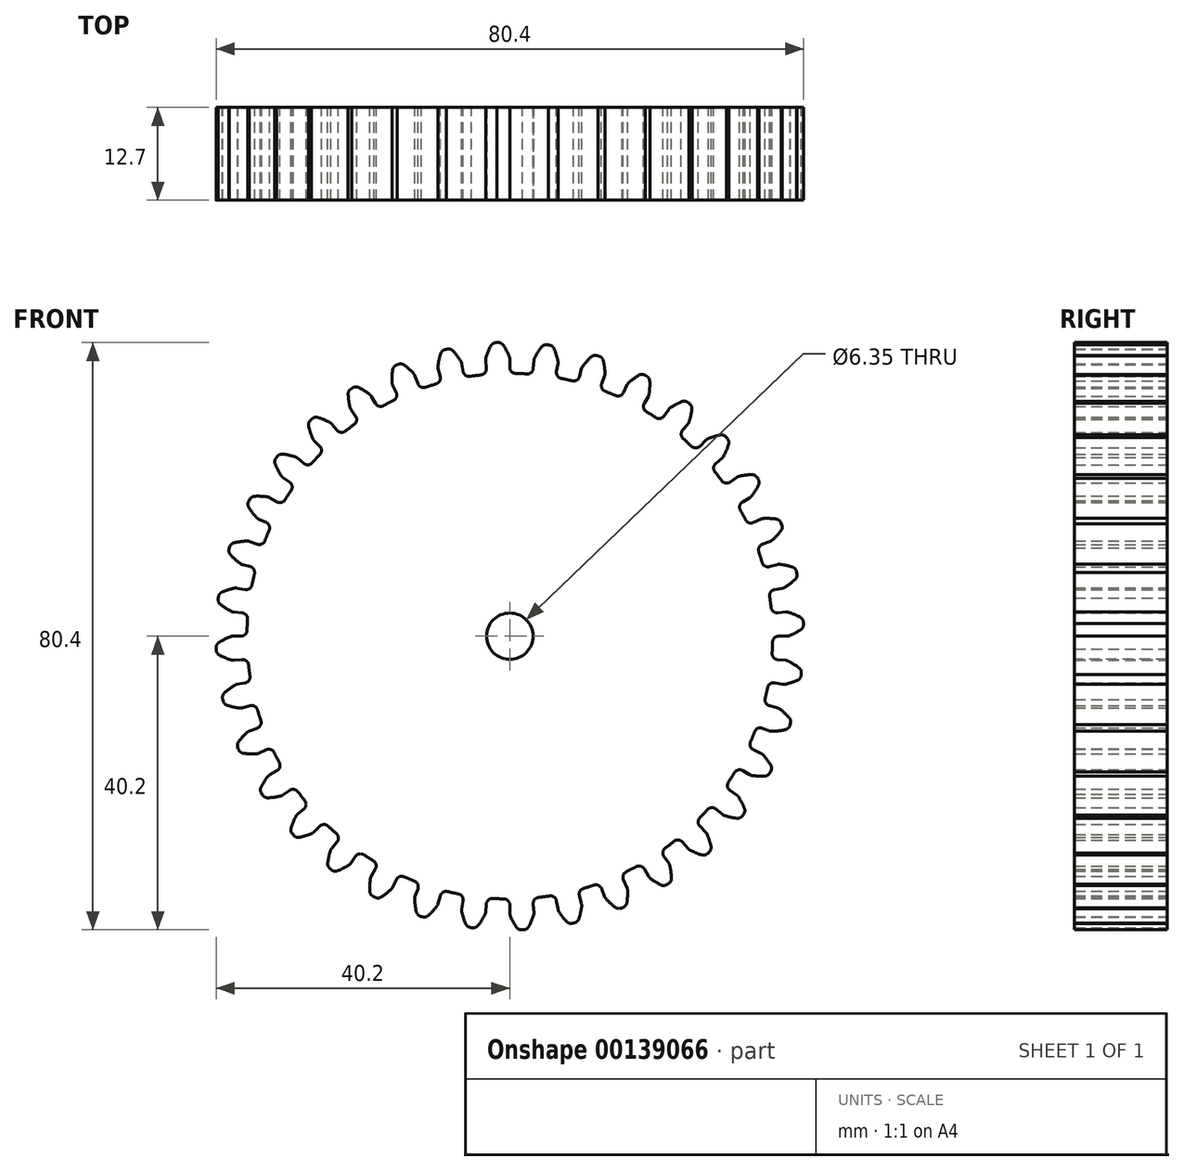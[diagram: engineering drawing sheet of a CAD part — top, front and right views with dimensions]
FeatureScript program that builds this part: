
annotation { "Feature Type Name" : "Feature", "Feature Type Description" : "" }
export const myFeature = defineFeature(function(context is Context, id is Id, definition is map)
    precondition{}
    {
        {
            var Q0;
            Q0=qCreatedBy(makeId("Front.planeOp"),FACE);
            var sketch = newSketch(context, id + "F0", { "sketchPlane" : qUnion([Q0])});
            skArc(sketch, "E0", {"start": v(-3.94, 35.77) * mm, "mid": v(-4.7, 35.68) * mm, "end": v(-5.45, 35.57) * mm});
            skLineSegment(sketch, "E1", {"start": v(-1.57, 40.2) * mm, "end": v(-1.76, 40.2) * mm});
            skLineSegment(sketch, "E2", {"start": v(0, 37.94) * mm, "end": v(0, 36.8) * mm});
            skArc(sketch, "E3.trimOffspring", {"start": v(-0.06, 38.25) * mm, "mid": v(-0.43, 39.06) * mm, "end": v(-0.87, 39.82) * mm});
            skLineSegment(sketch, "E4.MirrorCS", {"start": v(-1.94, 40.18) * mm, "end": v(-1.76, 40.2) * mm});
            skArc(sketch, "E5.MirrorCS", {"start": v(-3.27, 38.11) * mm, "mid": v(-2.98, 38.94) * mm, "end": v(-2.6, 39.75) * mm});
            skLineSegment(sketch, "E6.MirrorCS", {"start": v(-3.3, 37.8) * mm, "end": v(-3.2, 36.66) * mm});
            skPoint(sketch, "E7.visualSharp", {"position": v(0, 35.98) * mm});
            skArc(sketch, "E7.filletArc", {"start": v(0, 36.8) * mm, "mid": v(0.24, 36.22) * mm, "end": v(0.8, 35.97) * mm});
            skPoint(sketch, "E8.visualSharp", {"position": v(-3.14, 35.85) * mm});
            skArc(sketch, "E8.filletArc", {"start": v(-3.94, 35.77) * mm, "mid": v(-3.4, 36.06) * mm, "end": v(-3.2, 36.66) * mm});
            skPoint(sketch, "E9.visualSharp", {"position": v(-3.32, 37.96) * mm});
            skArc(sketch, "E9.filletArc", {"start": v(-3.27, 38.11) * mm, "mid": v(-3.3, 37.96) * mm, "end": v(-3.3, 37.8) * mm});
            skPoint(sketch, "E10.visualSharp", {"position": v(0, 38.1) * mm});
            skArc(sketch, "E10.filletArc", {"start": v(0, 37.94) * mm, "mid": v(-0.02, 38.1) * mm, "end": v(-0.06, 38.25) * mm});
            skPoint(sketch, "E11.visualSharp", {"position": v(-2.38, 40.15) * mm});
            skArc(sketch, "E11.filletArc", {"start": v(-1.94, 40.18) * mm, "mid": v(-2.33, 40.05) * mm, "end": v(-2.6, 39.75) * mm});
            skPoint(sketch, "E12.visualSharp", {"position": v(-1.13, 40.2) * mm});
            skArc(sketch, "E12.filletArc", {"start": v(-0.87, 39.82) * mm, "mid": v(-1.17, 40.1) * mm, "end": v(-1.57, 40.2) * mm});
            skArc(sketch, "E13.1.0", {"start": v(-10.1, 34.54) * mm, "mid": v(-9.6, 34.93) * mm, "end": v(-9.52, 35.55) * mm});
            skLineSegment(sketch, "E13.1.1", {"start": v(-9.82, 36.65) * mm, "end": v(-9.52, 35.55) * mm});
            skArc(sketch, "E13.1.2", {"start": v(-9.84, 36.96) * mm, "mid": v(-9.85, 36.8) * mm, "end": v(-9.82, 36.65) * mm});
            skArc(sketch, "E13.1.3", {"start": v(-9.84, 36.96) * mm, "mid": v(-9.7, 37.84) * mm, "end": v(-9.47, 38.69) * mm});
            skArc(sketch, "E13.1.4", {"start": v(-8.9, 39.24) * mm, "mid": v(-9.25, 39.04) * mm, "end": v(-9.47, 38.69) * mm});
            skLineSegment(sketch, "E13.1.5", {"start": v(-8.9, 39.24) * mm, "end": v(-8.7, 39.29) * mm});
            skLineSegment(sketch, "E13.1.6", {"start": v(-8.52, 39.32) * mm, "end": v(-8.7, 39.29) * mm});
            skArc(sketch, "E13.1.7", {"start": v(-7.77, 39.06) * mm, "mid": v(-8.12, 39.29) * mm, "end": v(-8.52, 39.32) * mm});
            skArc(sketch, "E13.1.8", {"start": v(-6.7, 37.66) * mm, "mid": v(-7.2, 38.39) * mm, "end": v(-7.77, 39.06) * mm});
            skArc(sketch, "E13.1.9", {"start": v(-6.59, 37.37) * mm, "mid": v(-6.63, 37.52) * mm, "end": v(-6.7, 37.66) * mm});
            skLineSegment(sketch, "E13.1.10", {"start": v(-6.59, 37.37) * mm, "end": v(-6.4, 36.24) * mm});
            skArc(sketch, "E13.1.11", {"start": v(-6.4, 36.24) * mm, "mid": v(-6.06, 35.71) * mm, "end": v(-5.45, 35.57) * mm});
            skArc(sketch, "E13.2.0", {"start": v(-15.93, 32.26) * mm, "mid": v(-15.52, 32.73) * mm, "end": v(-15.55, 33.35) * mm});
            skLineSegment(sketch, "E13.2.1", {"start": v(-16.04, 34.39) * mm, "end": v(-15.55, 33.35) * mm});
            skArc(sketch, "E13.2.2", {"start": v(-16.11, 34.7) * mm, "mid": v(-16.09, 34.54) * mm, "end": v(-16.04, 34.39) * mm});
            skArc(sketch, "E13.2.3", {"start": v(-16.11, 34.7) * mm, "mid": v(-16.12, 35.58) * mm, "end": v(-16.04, 36.46) * mm});
            skArc(sketch, "E13.2.4", {"start": v(-15.57, 37.1) * mm, "mid": v(-15.89, 36.84) * mm, "end": v(-16.04, 36.46) * mm});
            skLineSegment(sketch, "E13.2.5", {"start": v(-15.57, 37.1) * mm, "end": v(-15.4, 37.18) * mm});
            skLineSegment(sketch, "E13.2.6", {"start": v(-15.22, 37.24) * mm, "end": v(-15.4, 37.18) * mm});
            skArc(sketch, "E13.2.7", {"start": v(-14.44, 37.12) * mm, "mid": v(-14.81, 37.28) * mm, "end": v(-15.22, 37.24) * mm});
            skArc(sketch, "E13.2.8", {"start": v(-13.14, 35.93) * mm, "mid": v(-13.76, 36.55) * mm, "end": v(-14.44, 37.12) * mm});
            skArc(sketch, "E13.2.9", {"start": v(-12.98, 35.65) * mm, "mid": v(-13.05, 35.8) * mm, "end": v(-13.14, 35.93) * mm});
            skLineSegment(sketch, "E13.2.10", {"start": v(-12.98, 35.65) * mm, "end": v(-12.59, 34.58) * mm});
            skArc(sketch, "E13.2.11", {"start": v(-12.59, 34.58) * mm, "mid": v(-12.17, 34.12) * mm, "end": v(-11.55, 34.08) * mm});
            skArc(sketch, "E13.3.0", {"start": v(-21.3, 29) * mm, "mid": v(-20.97, 29.54) * mm, "end": v(-21.1, 30.14) * mm});
            skLineSegment(sketch, "E13.3.1", {"start": v(-21.76, 31.08) * mm, "end": v(-21.1, 30.14) * mm});
            skArc(sketch, "E13.3.2", {"start": v(-21.9, 31.37) * mm, "mid": v(-21.84, 31.22) * mm, "end": v(-21.76, 31.08) * mm});
            skArc(sketch, "E13.3.3", {"start": v(-21.9, 31.37) * mm, "mid": v(-22.05, 32.24) * mm, "end": v(-22.13, 33.12) * mm});
            skArc(sketch, "E13.3.4", {"start": v(-21.78, 33.83) * mm, "mid": v(-22.04, 33.52) * mm, "end": v(-22.13, 33.12) * mm});
            skLineSegment(sketch, "E13.3.5", {"start": v(-21.78, 33.83) * mm, "end": v(-21.62, 33.94) * mm});
            skLineSegment(sketch, "E13.3.6", {"start": v(-21.46, 34.03) * mm, "end": v(-21.62, 33.94) * mm});
            skArc(sketch, "E13.3.7", {"start": v(-20.66, 34.05) * mm, "mid": v(-21.06, 34.14) * mm, "end": v(-21.46, 34.03) * mm});
            skArc(sketch, "E13.3.8", {"start": v(-19.18, 33.1) * mm, "mid": v(-19.9, 33.6) * mm, "end": v(-20.66, 34.05) * mm});
            skArc(sketch, "E13.3.9", {"start": v(-18.97, 32.86) * mm, "mid": v(-19.06, 32.99) * mm, "end": v(-19.18, 33.1) * mm});
            skLineSegment(sketch, "E13.3.10", {"start": v(-18.97, 32.86) * mm, "end": v(-18.4, 31.87) * mm});
            skArc(sketch, "E13.3.11", {"start": v(-18.4, 31.87) * mm, "mid": v(-17.9, 31.49) * mm, "end": v(-17.29, 31.56) * mm});
            skArc(sketch, "E13.4.0", {"start": v(-26, 24.87) * mm, "mid": v(-25.78, 25.45) * mm, "end": v(-26.02, 26.02) * mm});
            skLineSegment(sketch, "E13.4.1", {"start": v(-26.83, 26.83) * mm, "end": v(-26.02, 26.02) * mm});
            skArc(sketch, "E13.4.2", {"start": v(-27, 27.1) * mm, "mid": v(-26.93, 26.95) * mm, "end": v(-26.83, 26.83) * mm});
            skArc(sketch, "E13.4.3", {"start": v(-27, 27.1) * mm, "mid": v(-27.31, 27.92) * mm, "end": v(-27.54, 28.77) * mm});
            skArc(sketch, "E13.4.4", {"start": v(-27.32, 29.53) * mm, "mid": v(-27.53, 29.18) * mm, "end": v(-27.54, 28.77) * mm});
            skLineSegment(sketch, "E13.4.5", {"start": v(-27.32, 29.53) * mm, "end": v(-27.19, 29.67) * mm});
            skLineSegment(sketch, "E13.4.6", {"start": v(-27.04, 29.79) * mm, "end": v(-27.19, 29.67) * mm});
            skArc(sketch, "E13.4.7", {"start": v(-26.26, 29.94) * mm, "mid": v(-26.67, 29.97) * mm, "end": v(-27.04, 29.79) * mm});
            skArc(sketch, "E13.4.8", {"start": v(-24.63, 29.26) * mm, "mid": v(-25.43, 29.64) * mm, "end": v(-26.26, 29.94) * mm});
            skArc(sketch, "E13.4.9", {"start": v(-24.39, 29.07) * mm, "mid": v(-24.5, 29.18) * mm, "end": v(-24.63, 29.26) * mm});
            skLineSegment(sketch, "E13.4.10", {"start": v(-24.39, 29.07) * mm, "end": v(-23.65, 28.2) * mm});
            skArc(sketch, "E13.4.11", {"start": v(-23.65, 28.2) * mm, "mid": v(-23.1, 27.9) * mm, "end": v(-22.5, 28.08) * mm});
            skArc(sketch, "E13.5.0", {"start": v(-29.93, 19.97) * mm, "mid": v(-29.8, 20.58) * mm, "end": v(-30.14, 21.1) * mm});
            skLineSegment(sketch, "E13.5.1", {"start": v(-31.08, 21.76) * mm, "end": v(-30.14, 21.1) * mm});
            skArc(sketch, "E13.5.2", {"start": v(-31.3, 22) * mm, "mid": v(-31.2, 21.87) * mm, "end": v(-31.08, 21.76) * mm});
            skArc(sketch, "E13.5.3", {"start": v(-31.3, 22) * mm, "mid": v(-31.75, 22.75) * mm, "end": v(-32.12, 23.55) * mm});
            skArc(sketch, "E13.5.4", {"start": v(-32.03, 24.34) * mm, "mid": v(-32.18, 23.96) * mm, "end": v(-32.12, 23.55) * mm});
            skLineSegment(sketch, "E13.5.5", {"start": v(-32.03, 24.34) * mm, "end": v(-31.92, 24.5) * mm});
            skLineSegment(sketch, "E13.5.6", {"start": v(-31.8, 24.64) * mm, "end": v(-31.92, 24.5) * mm});
            skArc(sketch, "E13.5.7", {"start": v(-31.06, 24.93) * mm, "mid": v(-31.47, 24.88) * mm, "end": v(-31.8, 24.64) * mm});
            skArc(sketch, "E13.5.8", {"start": v(-29.34, 24.54) * mm, "mid": v(-30.2, 24.78) * mm, "end": v(-31.06, 24.93) * mm});
            skArc(sketch, "E13.5.9", {"start": v(-29.07, 24.39) * mm, "mid": v(-29.2, 24.48) * mm, "end": v(-29.34, 24.54) * mm});
            skLineSegment(sketch, "E13.5.10", {"start": v(-29.07, 24.39) * mm, "end": v(-28.2, 23.65) * mm});
            skArc(sketch, "E13.5.11", {"start": v(-28.2, 23.65) * mm, "mid": v(-27.6, 23.46) * mm, "end": v(-27.04, 23.74) * mm});
            skArc(sketch, "E13.6.0", {"start": v(-32.94, 14.47) * mm, "mid": v(-32.93, 15.1) * mm, "end": v(-33.35, 15.55) * mm});
            skLineSegment(sketch, "E13.6.1", {"start": v(-34.39, 16.04) * mm, "end": v(-33.35, 15.55) * mm});
            skArc(sketch, "E13.6.2", {"start": v(-34.64, 16.22) * mm, "mid": v(-34.52, 16.12) * mm, "end": v(-34.39, 16.04) * mm});
            skArc(sketch, "E13.6.3", {"start": v(-34.64, 16.22) * mm, "mid": v(-35.21, 16.9) * mm, "end": v(-35.72, 17.62) * mm});
            skArc(sketch, "E13.6.4", {"start": v(-35.77, 18.4) * mm, "mid": v(-35.85, 18) * mm, "end": v(-35.72, 17.62) * mm});
            skLineSegment(sketch, "E13.6.5", {"start": v(-35.77, 18.4) * mm, "end": v(-35.7, 18.58) * mm});
            skLineSegment(sketch, "E13.6.6", {"start": v(-35.6, 18.74) * mm, "end": v(-35.7, 18.58) * mm});
            skArc(sketch, "E13.6.7", {"start": v(-34.92, 19.16) * mm, "mid": v(-35.31, 19.04) * mm, "end": v(-35.6, 18.74) * mm});
            skArc(sketch, "E13.6.8", {"start": v(-33.16, 19.07) * mm, "mid": v(-34.04, 19.16) * mm, "end": v(-34.92, 19.16) * mm});
            skArc(sketch, "E13.6.9", {"start": v(-32.86, 18.97) * mm, "mid": v(-33, 19.04) * mm, "end": v(-33.16, 19.07) * mm});
            skLineSegment(sketch, "E13.6.10", {"start": v(-32.86, 18.97) * mm, "end": v(-31.87, 18.4) * mm});
            skArc(sketch, "E13.6.11", {"start": v(-31.87, 18.4) * mm, "mid": v(-31.25, 18.31) * mm, "end": v(-30.75, 18.69) * mm});
            skArc(sketch, "E13.7.0", {"start": v(-34.96, 8.53) * mm, "mid": v(-35.05, 9.15) * mm, "end": v(-35.55, 9.52) * mm});
            skLineSegment(sketch, "E13.7.1", {"start": v(-36.65, 9.82) * mm, "end": v(-35.55, 9.52) * mm});
            skArc(sketch, "E13.7.2", {"start": v(-36.93, 9.96) * mm, "mid": v(-36.8, 9.88) * mm, "end": v(-36.65, 9.82) * mm});
            skArc(sketch, "E13.7.3", {"start": v(-36.93, 9.96) * mm, "mid": v(-37.61, 10.52) * mm, "end": v(-38.24, 11.15) * mm});
            skArc(sketch, "E13.7.4", {"start": v(-38.43, 11.92) * mm, "mid": v(-38.43, 11.5) * mm, "end": v(-38.24, 11.15) * mm});
            skLineSegment(sketch, "E13.7.5", {"start": v(-38.43, 11.92) * mm, "end": v(-38.38, 12.1) * mm});
            skLineSegment(sketch, "E13.7.6", {"start": v(-38.31, 12.28) * mm, "end": v(-38.38, 12.1) * mm});
            skArc(sketch, "E13.7.7", {"start": v(-37.72, 12.8) * mm, "mid": v(-38.08, 12.62) * mm, "end": v(-38.31, 12.28) * mm});
            skArc(sketch, "E13.7.8", {"start": v(-35.97, 13.03) * mm, "mid": v(-36.85, 12.95) * mm, "end": v(-37.72, 12.8) * mm});
            skArc(sketch, "E13.7.9", {"start": v(-35.65, 12.98) * mm, "mid": v(-35.8, 13.02) * mm, "end": v(-35.97, 13.03) * mm});
            skLineSegment(sketch, "E13.7.10", {"start": v(-35.65, 12.98) * mm, "end": v(-34.58, 12.59) * mm});
            skArc(sketch, "E13.7.11", {"start": v(-34.58, 12.59) * mm, "mid": v(-33.96, 12.6) * mm, "end": v(-33.53, 13.06) * mm});
            skArc(sketch, "E13.8.0", {"start": v(-35.9, 2.33) * mm, "mid": v(-36.1, 2.92) * mm, "end": v(-36.66, 3.2) * mm});
            skLineSegment(sketch, "E13.8.1", {"start": v(-37.8, 3.3) * mm, "end": v(-36.66, 3.2) * mm});
            skArc(sketch, "E13.8.2", {"start": v(-38.1, 3.4) * mm, "mid": v(-37.95, 3.34) * mm, "end": v(-37.8, 3.3) * mm});
            skArc(sketch, "E13.8.3", {"start": v(-38.1, 3.4) * mm, "mid": v(-38.87, 3.83) * mm, "end": v(-39.6, 4.34) * mm});
            skArc(sketch, "E13.8.4", {"start": v(-39.91, 5.06) * mm, "mid": v(-39.85, 4.66) * mm, "end": v(-39.6, 4.34) * mm});
            skLineSegment(sketch, "E13.8.5", {"start": v(-39.91, 5.06) * mm, "end": v(-39.9, 5.25) * mm});
            skLineSegment(sketch, "E13.8.6", {"start": v(-39.86, 5.44) * mm, "end": v(-39.9, 5.25) * mm});
            skArc(sketch, "E13.8.7", {"start": v(-39.37, 6.06) * mm, "mid": v(-39.7, 5.81) * mm, "end": v(-39.86, 5.44) * mm});
            skArc(sketch, "E13.8.8", {"start": v(-37.68, 6.58) * mm, "mid": v(-38.54, 6.36) * mm, "end": v(-39.37, 6.06) * mm});
            skArc(sketch, "E13.8.9", {"start": v(-37.37, 6.59) * mm, "mid": v(-37.52, 6.6) * mm, "end": v(-37.68, 6.58) * mm});
            skLineSegment(sketch, "E13.8.10", {"start": v(-37.37, 6.59) * mm, "end": v(-36.24, 6.4) * mm});
            skArc(sketch, "E13.8.11", {"start": v(-36.24, 6.4) * mm, "mid": v(-35.63, 6.52) * mm, "end": v(-35.29, 7.04) * mm});
            skArc(sketch, "E13.9.0", {"start": v(-35.77, -3.94) * mm, "mid": v(-36.06, -3.4) * mm, "end": v(-36.66, -3.2) * mm});
            skLineSegment(sketch, "E13.9.1", {"start": v(-37.8, -3.3) * mm, "end": v(-36.66, -3.2) * mm});
            skArc(sketch, "E13.9.2", {"start": v(-38.11, -3.27) * mm, "mid": v(-37.96, -3.3) * mm, "end": v(-37.8, -3.3) * mm});
            skArc(sketch, "E13.9.3", {"start": v(-38.11, -3.27) * mm, "mid": v(-38.94, -2.98) * mm, "end": v(-39.75, -2.6) * mm});
            skArc(sketch, "E13.9.4", {"start": v(-40.18, -1.94) * mm, "mid": v(-40.05, -2.33) * mm, "end": v(-39.75, -2.6) * mm});
            skLineSegment(sketch, "E13.9.5", {"start": v(-40.18, -1.94) * mm, "end": v(-40.2, -1.76) * mm});
            skLineSegment(sketch, "E13.9.6", {"start": v(-40.2, -1.57) * mm, "end": v(-40.2, -1.76) * mm});
            skArc(sketch, "E13.9.7", {"start": v(-39.82, -0.87) * mm, "mid": v(-40.1, -1.17) * mm, "end": v(-40.2, -1.57) * mm});
            skArc(sketch, "E13.9.8", {"start": v(-38.25, -0.06) * mm, "mid": v(-39.06, -0.43) * mm, "end": v(-39.82, -0.87) * mm});
            skArc(sketch, "E13.9.9", {"start": v(-37.94, 0) * mm, "mid": v(-38.1, -0.02) * mm, "end": v(-38.25, -0.06) * mm});
            skLineSegment(sketch, "E13.9.10", {"start": v(-37.94, 0) * mm, "end": v(-36.8, 0) * mm});
            skArc(sketch, "E13.9.11", {"start": v(-36.8, 0) * mm, "mid": v(-36.22, 0.24) * mm, "end": v(-35.97, 0.8) * mm});
            skArc(sketch, "E13.10.0", {"start": v(-34.54, -10.1) * mm, "mid": v(-34.93, -9.6) * mm, "end": v(-35.55, -9.52) * mm});
            skLineSegment(sketch, "E13.10.1", {"start": v(-36.65, -9.82) * mm, "end": v(-35.55, -9.52) * mm});
            skArc(sketch, "E13.10.2", {"start": v(-36.96, -9.84) * mm, "mid": v(-36.8, -9.85) * mm, "end": v(-36.65, -9.82) * mm});
            skArc(sketch, "E13.10.3", {"start": v(-36.96, -9.84) * mm, "mid": v(-37.84, -9.7) * mm, "end": v(-38.69, -9.47) * mm});
            skArc(sketch, "E13.10.4", {"start": v(-39.24, -8.9) * mm, "mid": v(-39.04, -9.25) * mm, "end": v(-38.69, -9.47) * mm});
            skLineSegment(sketch, "E13.10.5", {"start": v(-39.24, -8.9) * mm, "end": v(-39.29, -8.7) * mm});
            skLineSegment(sketch, "E13.10.6", {"start": v(-39.32, -8.52) * mm, "end": v(-39.29, -8.7) * mm});
            skArc(sketch, "E13.10.7", {"start": v(-39.06, -7.77) * mm, "mid": v(-39.29, -8.12) * mm, "end": v(-39.32, -8.52) * mm});
            skArc(sketch, "E13.10.8", {"start": v(-37.66, -6.7) * mm, "mid": v(-38.39, -7.2) * mm, "end": v(-39.06, -7.77) * mm});
            skArc(sketch, "E13.10.9", {"start": v(-37.37, -6.59) * mm, "mid": v(-37.52, -6.63) * mm, "end": v(-37.66, -6.7) * mm});
            skLineSegment(sketch, "E13.10.10", {"start": v(-37.37, -6.59) * mm, "end": v(-36.24, -6.4) * mm});
            skArc(sketch, "E13.10.11", {"start": v(-36.24, -6.4) * mm, "mid": v(-35.71, -6.06) * mm, "end": v(-35.57, -5.45) * mm});
            skArc(sketch, "E13.11.0", {"start": v(-32.26, -15.93) * mm, "mid": v(-32.73, -15.52) * mm, "end": v(-33.35, -15.55) * mm});
            skLineSegment(sketch, "E13.11.1", {"start": v(-34.39, -16.04) * mm, "end": v(-33.35, -15.55) * mm});
            skArc(sketch, "E13.11.2", {"start": v(-34.7, -16.11) * mm, "mid": v(-34.54, -16.09) * mm, "end": v(-34.39, -16.04) * mm});
            skArc(sketch, "E13.11.3", {"start": v(-34.7, -16.11) * mm, "mid": v(-35.58, -16.12) * mm, "end": v(-36.46, -16.04) * mm});
            skArc(sketch, "E13.11.4", {"start": v(-37.1, -15.57) * mm, "mid": v(-36.84, -15.89) * mm, "end": v(-36.46, -16.04) * mm});
            skLineSegment(sketch, "E13.11.5", {"start": v(-37.1, -15.57) * mm, "end": v(-37.18, -15.4) * mm});
            skLineSegment(sketch, "E13.11.6", {"start": v(-37.24, -15.22) * mm, "end": v(-37.18, -15.4) * mm});
            skArc(sketch, "E13.11.7", {"start": v(-37.12, -14.44) * mm, "mid": v(-37.28, -14.81) * mm, "end": v(-37.24, -15.22) * mm});
            skArc(sketch, "E13.11.8", {"start": v(-35.93, -13.14) * mm, "mid": v(-36.55, -13.76) * mm, "end": v(-37.12, -14.44) * mm});
            skArc(sketch, "E13.11.9", {"start": v(-35.65, -12.98) * mm, "mid": v(-35.8, -13.05) * mm, "end": v(-35.93, -13.14) * mm});
            skLineSegment(sketch, "E13.11.10", {"start": v(-35.65, -12.98) * mm, "end": v(-34.58, -12.59) * mm});
            skArc(sketch, "E13.11.11", {"start": v(-34.58, -12.59) * mm, "mid": v(-34.12, -12.17) * mm, "end": v(-34.08, -11.55) * mm});
            skArc(sketch, "E13.12.0", {"start": v(-29, -21.3) * mm, "mid": v(-29.54, -20.97) * mm, "end": v(-30.14, -21.1) * mm});
            skLineSegment(sketch, "E13.12.1", {"start": v(-31.08, -21.76) * mm, "end": v(-30.14, -21.1) * mm});
            skArc(sketch, "E13.12.2", {"start": v(-31.37, -21.9) * mm, "mid": v(-31.22, -21.84) * mm, "end": v(-31.08, -21.76) * mm});
            skArc(sketch, "E13.12.3", {"start": v(-31.37, -21.9) * mm, "mid": v(-32.24, -22.05) * mm, "end": v(-33.12, -22.13) * mm});
            skArc(sketch, "E13.12.4", {"start": v(-33.83, -21.78) * mm, "mid": v(-33.52, -22.04) * mm, "end": v(-33.12, -22.13) * mm});
            skLineSegment(sketch, "E13.12.5", {"start": v(-33.83, -21.78) * mm, "end": v(-33.94, -21.62) * mm});
            skLineSegment(sketch, "E13.12.6", {"start": v(-34.03, -21.46) * mm, "end": v(-33.94, -21.62) * mm});
            skArc(sketch, "E13.12.7", {"start": v(-34.05, -20.66) * mm, "mid": v(-34.14, -21.06) * mm, "end": v(-34.03, -21.46) * mm});
            skArc(sketch, "E13.12.8", {"start": v(-33.1, -19.18) * mm, "mid": v(-33.6, -19.9) * mm, "end": v(-34.05, -20.66) * mm});
            skArc(sketch, "E13.12.9", {"start": v(-32.86, -18.97) * mm, "mid": v(-32.99, -19.06) * mm, "end": v(-33.1, -19.18) * mm});
            skLineSegment(sketch, "E13.12.10", {"start": v(-32.86, -18.97) * mm, "end": v(-31.87, -18.4) * mm});
            skArc(sketch, "E13.12.11", {"start": v(-31.87, -18.4) * mm, "mid": v(-31.49, -17.9) * mm, "end": v(-31.56, -17.29) * mm});
            skArc(sketch, "E13.13.0", {"start": v(-24.87, -26) * mm, "mid": v(-25.45, -25.78) * mm, "end": v(-26.02, -26.02) * mm});
            skLineSegment(sketch, "E13.13.1", {"start": v(-26.83, -26.83) * mm, "end": v(-26.02, -26.02) * mm});
            skArc(sketch, "E13.13.2", {"start": v(-27.1, -27) * mm, "mid": v(-26.95, -26.93) * mm, "end": v(-26.83, -26.83) * mm});
            skArc(sketch, "E13.13.3", {"start": v(-27.1, -27) * mm, "mid": v(-27.92, -27.31) * mm, "end": v(-28.77, -27.54) * mm});
            skArc(sketch, "E13.13.4", {"start": v(-29.53, -27.32) * mm, "mid": v(-29.18, -27.53) * mm, "end": v(-28.77, -27.54) * mm});
            skLineSegment(sketch, "E13.13.5", {"start": v(-29.53, -27.32) * mm, "end": v(-29.67, -27.19) * mm});
            skLineSegment(sketch, "E13.13.6", {"start": v(-29.79, -27.04) * mm, "end": v(-29.67, -27.19) * mm});
            skArc(sketch, "E13.13.7", {"start": v(-29.94, -26.26) * mm, "mid": v(-29.97, -26.67) * mm, "end": v(-29.79, -27.04) * mm});
            skArc(sketch, "E13.13.8", {"start": v(-29.26, -24.63) * mm, "mid": v(-29.64, -25.43) * mm, "end": v(-29.94, -26.26) * mm});
            skArc(sketch, "E13.13.9", {"start": v(-29.07, -24.39) * mm, "mid": v(-29.18, -24.5) * mm, "end": v(-29.26, -24.63) * mm});
            skLineSegment(sketch, "E13.13.10", {"start": v(-29.07, -24.39) * mm, "end": v(-28.2, -23.65) * mm});
            skArc(sketch, "E13.13.11", {"start": v(-28.2, -23.65) * mm, "mid": v(-27.9, -23.1) * mm, "end": v(-28.08, -22.5) * mm});
            skArc(sketch, "E13.14.0", {"start": v(-19.97, -29.93) * mm, "mid": v(-20.58, -29.8) * mm, "end": v(-21.1, -30.14) * mm});
            skLineSegment(sketch, "E13.14.1", {"start": v(-21.76, -31.08) * mm, "end": v(-21.1, -30.14) * mm});
            skArc(sketch, "E13.14.2", {"start": v(-22, -31.3) * mm, "mid": v(-21.87, -31.2) * mm, "end": v(-21.76, -31.08) * mm});
            skArc(sketch, "E13.14.3", {"start": v(-22, -31.3) * mm, "mid": v(-22.75, -31.75) * mm, "end": v(-23.55, -32.12) * mm});
            skArc(sketch, "E13.14.4", {"start": v(-24.34, -32.03) * mm, "mid": v(-23.96, -32.18) * mm, "end": v(-23.55, -32.12) * mm});
            skLineSegment(sketch, "E13.14.5", {"start": v(-24.34, -32.03) * mm, "end": v(-24.5, -31.92) * mm});
            skLineSegment(sketch, "E13.14.6", {"start": v(-24.64, -31.8) * mm, "end": v(-24.5, -31.92) * mm});
            skArc(sketch, "E13.14.7", {"start": v(-24.93, -31.06) * mm, "mid": v(-24.88, -31.47) * mm, "end": v(-24.64, -31.8) * mm});
            skArc(sketch, "E13.14.8", {"start": v(-24.54, -29.34) * mm, "mid": v(-24.78, -30.2) * mm, "end": v(-24.93, -31.06) * mm});
            skArc(sketch, "E13.14.9", {"start": v(-24.39, -29.07) * mm, "mid": v(-24.48, -29.2) * mm, "end": v(-24.54, -29.34) * mm});
            skLineSegment(sketch, "E13.14.10", {"start": v(-24.39, -29.07) * mm, "end": v(-23.65, -28.2) * mm});
            skArc(sketch, "E13.14.11", {"start": v(-23.65, -28.2) * mm, "mid": v(-23.46, -27.6) * mm, "end": v(-23.74, -27.04) * mm});
            skArc(sketch, "E13.15.0", {"start": v(-14.47, -32.94) * mm, "mid": v(-15.1, -32.93) * mm, "end": v(-15.55, -33.35) * mm});
            skLineSegment(sketch, "E13.15.1", {"start": v(-16.04, -34.39) * mm, "end": v(-15.55, -33.35) * mm});
            skArc(sketch, "E13.15.2", {"start": v(-16.22, -34.64) * mm, "mid": v(-16.12, -34.52) * mm, "end": v(-16.04, -34.39) * mm});
            skArc(sketch, "E13.15.3", {"start": v(-16.22, -34.64) * mm, "mid": v(-16.9, -35.21) * mm, "end": v(-17.62, -35.72) * mm});
            skArc(sketch, "E13.15.4", {"start": v(-18.4, -35.77) * mm, "mid": v(-18, -35.85) * mm, "end": v(-17.62, -35.72) * mm});
            skLineSegment(sketch, "E13.15.5", {"start": v(-18.4, -35.77) * mm, "end": v(-18.58, -35.7) * mm});
            skLineSegment(sketch, "E13.15.6", {"start": v(-18.74, -35.6) * mm, "end": v(-18.58, -35.7) * mm});
            skArc(sketch, "E13.15.7", {"start": v(-19.16, -34.92) * mm, "mid": v(-19.04, -35.31) * mm, "end": v(-18.74, -35.6) * mm});
            skArc(sketch, "E13.15.8", {"start": v(-19.07, -33.16) * mm, "mid": v(-19.16, -34.04) * mm, "end": v(-19.16, -34.92) * mm});
            skArc(sketch, "E13.15.9", {"start": v(-18.97, -32.86) * mm, "mid": v(-19.04, -33) * mm, "end": v(-19.07, -33.16) * mm});
            skLineSegment(sketch, "E13.15.10", {"start": v(-18.97, -32.86) * mm, "end": v(-18.4, -31.87) * mm});
            skArc(sketch, "E13.15.11", {"start": v(-18.4, -31.87) * mm, "mid": v(-18.31, -31.25) * mm, "end": v(-18.69, -30.75) * mm});
            skArc(sketch, "E13.16.0", {"start": v(-8.53, -34.96) * mm, "mid": v(-9.15, -35.05) * mm, "end": v(-9.52, -35.55) * mm});
            skLineSegment(sketch, "E13.16.1", {"start": v(-9.82, -36.65) * mm, "end": v(-9.52, -35.55) * mm});
            skArc(sketch, "E13.16.2", {"start": v(-9.96, -36.93) * mm, "mid": v(-9.88, -36.8) * mm, "end": v(-9.82, -36.65) * mm});
            skArc(sketch, "E13.16.3", {"start": v(-9.96, -36.93) * mm, "mid": v(-10.52, -37.61) * mm, "end": v(-11.15, -38.24) * mm});
            skArc(sketch, "E13.16.4", {"start": v(-11.92, -38.43) * mm, "mid": v(-11.5, -38.43) * mm, "end": v(-11.15, -38.24) * mm});
            skLineSegment(sketch, "E13.16.5", {"start": v(-11.92, -38.43) * mm, "end": v(-12.1, -38.38) * mm});
            skLineSegment(sketch, "E13.16.6", {"start": v(-12.28, -38.31) * mm, "end": v(-12.1, -38.38) * mm});
            skArc(sketch, "E13.16.7", {"start": v(-12.8, -37.72) * mm, "mid": v(-12.62, -38.08) * mm, "end": v(-12.28, -38.31) * mm});
            skArc(sketch, "E13.16.8", {"start": v(-13.03, -35.97) * mm, "mid": v(-12.95, -36.85) * mm, "end": v(-12.8, -37.72) * mm});
            skArc(sketch, "E13.16.9", {"start": v(-12.98, -35.65) * mm, "mid": v(-13.02, -35.8) * mm, "end": v(-13.03, -35.97) * mm});
            skLineSegment(sketch, "E13.16.10", {"start": v(-12.98, -35.65) * mm, "end": v(-12.59, -34.58) * mm});
            skArc(sketch, "E13.16.11", {"start": v(-12.59, -34.58) * mm, "mid": v(-12.6, -33.96) * mm, "end": v(-13.06, -33.53) * mm});
            skArc(sketch, "E13.17.0", {"start": v(-2.33, -35.9) * mm, "mid": v(-2.92, -36.1) * mm, "end": v(-3.2, -36.66) * mm});
            skLineSegment(sketch, "E13.17.1", {"start": v(-3.3, -37.8) * mm, "end": v(-3.2, -36.66) * mm});
            skArc(sketch, "E13.17.2", {"start": v(-3.4, -38.1) * mm, "mid": v(-3.34, -37.95) * mm, "end": v(-3.3, -37.8) * mm});
            skArc(sketch, "E13.17.3", {"start": v(-3.4, -38.1) * mm, "mid": v(-3.83, -38.87) * mm, "end": v(-4.34, -39.6) * mm});
            skArc(sketch, "E13.17.4", {"start": v(-5.06, -39.91) * mm, "mid": v(-4.66, -39.85) * mm, "end": v(-4.34, -39.6) * mm});
            skLineSegment(sketch, "E13.17.5", {"start": v(-5.06, -39.91) * mm, "end": v(-5.25, -39.9) * mm});
            skLineSegment(sketch, "E13.17.6", {"start": v(-5.44, -39.86) * mm, "end": v(-5.25, -39.9) * mm});
            skArc(sketch, "E13.17.7", {"start": v(-6.06, -39.37) * mm, "mid": v(-5.81, -39.7) * mm, "end": v(-5.44, -39.86) * mm});
            skArc(sketch, "E13.17.8", {"start": v(-6.58, -37.68) * mm, "mid": v(-6.36, -38.54) * mm, "end": v(-6.06, -39.37) * mm});
            skArc(sketch, "E13.17.9", {"start": v(-6.59, -37.37) * mm, "mid": v(-6.6, -37.52) * mm, "end": v(-6.58, -37.68) * mm});
            skLineSegment(sketch, "E13.17.10", {"start": v(-6.59, -37.37) * mm, "end": v(-6.4, -36.24) * mm});
            skArc(sketch, "E13.17.11", {"start": v(-6.4, -36.24) * mm, "mid": v(-6.52, -35.63) * mm, "end": v(-7.04, -35.29) * mm});
            skArc(sketch, "E13.18.0", {"start": v(3.94, -35.77) * mm, "mid": v(3.4, -36.06) * mm, "end": v(3.2, -36.66) * mm});
            skLineSegment(sketch, "E13.18.1", {"start": v(3.3, -37.8) * mm, "end": v(3.2, -36.66) * mm});
            skArc(sketch, "E13.18.2", {"start": v(3.27, -38.11) * mm, "mid": v(3.3, -37.96) * mm, "end": v(3.3, -37.8) * mm});
            skArc(sketch, "E13.18.3", {"start": v(3.27, -38.11) * mm, "mid": v(2.98, -38.94) * mm, "end": v(2.6, -39.75) * mm});
            skArc(sketch, "E13.18.4", {"start": v(1.94, -40.18) * mm, "mid": v(2.33, -40.05) * mm, "end": v(2.6, -39.75) * mm});
            skLineSegment(sketch, "E13.18.5", {"start": v(1.94, -40.18) * mm, "end": v(1.76, -40.2) * mm});
            skLineSegment(sketch, "E13.18.6", {"start": v(1.57, -40.2) * mm, "end": v(1.76, -40.2) * mm});
            skArc(sketch, "E13.18.7", {"start": v(0.87, -39.82) * mm, "mid": v(1.17, -40.1) * mm, "end": v(1.57, -40.2) * mm});
            skArc(sketch, "E13.18.8", {"start": v(0.06, -38.25) * mm, "mid": v(0.43, -39.06) * mm, "end": v(0.87, -39.82) * mm});
            skArc(sketch, "E13.18.9", {"start": v(0, -37.94) * mm, "mid": v(0.02, -38.1) * mm, "end": v(0.06, -38.25) * mm});
            skLineSegment(sketch, "E13.18.10", {"start": v(0, -37.94) * mm, "end": v(0, -36.8) * mm});
            skArc(sketch, "E13.18.11", {"start": v(0, -36.8) * mm, "mid": v(-0.24, -36.22) * mm, "end": v(-0.8, -35.97) * mm});
            skArc(sketch, "E13.19.0", {"start": v(10.1, -34.54) * mm, "mid": v(9.6, -34.93) * mm, "end": v(9.52, -35.55) * mm});
            skLineSegment(sketch, "E13.19.1", {"start": v(9.82, -36.65) * mm, "end": v(9.52, -35.55) * mm});
            skArc(sketch, "E13.19.2", {"start": v(9.84, -36.96) * mm, "mid": v(9.85, -36.8) * mm, "end": v(9.82, -36.65) * mm});
            skArc(sketch, "E13.19.3", {"start": v(9.84, -36.96) * mm, "mid": v(9.7, -37.84) * mm, "end": v(9.47, -38.69) * mm});
            skArc(sketch, "E13.19.4", {"start": v(8.9, -39.24) * mm, "mid": v(9.25, -39.04) * mm, "end": v(9.47, -38.69) * mm});
            skLineSegment(sketch, "E13.19.5", {"start": v(8.9, -39.24) * mm, "end": v(8.7, -39.29) * mm});
            skLineSegment(sketch, "E13.19.6", {"start": v(8.52, -39.32) * mm, "end": v(8.7, -39.29) * mm});
            skArc(sketch, "E13.19.7", {"start": v(7.77, -39.06) * mm, "mid": v(8.12, -39.29) * mm, "end": v(8.52, -39.32) * mm});
            skArc(sketch, "E13.19.8", {"start": v(6.7, -37.66) * mm, "mid": v(7.2, -38.39) * mm, "end": v(7.77, -39.06) * mm});
            skArc(sketch, "E13.19.9", {"start": v(6.59, -37.37) * mm, "mid": v(6.63, -37.52) * mm, "end": v(6.7, -37.66) * mm});
            skLineSegment(sketch, "E13.19.10", {"start": v(6.59, -37.37) * mm, "end": v(6.4, -36.24) * mm});
            skArc(sketch, "E13.19.11", {"start": v(6.4, -36.24) * mm, "mid": v(6.06, -35.71) * mm, "end": v(5.45, -35.57) * mm});
            skArc(sketch, "E13.20.0", {"start": v(15.93, -32.26) * mm, "mid": v(15.52, -32.73) * mm, "end": v(15.55, -33.35) * mm});
            skLineSegment(sketch, "E13.20.1", {"start": v(16.04, -34.39) * mm, "end": v(15.55, -33.35) * mm});
            skArc(sketch, "E13.20.2", {"start": v(16.11, -34.7) * mm, "mid": v(16.09, -34.54) * mm, "end": v(16.04, -34.39) * mm});
            skArc(sketch, "E13.20.3", {"start": v(16.11, -34.7) * mm, "mid": v(16.12, -35.58) * mm, "end": v(16.04, -36.46) * mm});
            skArc(sketch, "E13.20.4", {"start": v(15.57, -37.1) * mm, "mid": v(15.89, -36.84) * mm, "end": v(16.04, -36.46) * mm});
            skLineSegment(sketch, "E13.20.5", {"start": v(15.57, -37.1) * mm, "end": v(15.4, -37.18) * mm});
            skLineSegment(sketch, "E13.20.6", {"start": v(15.22, -37.24) * mm, "end": v(15.4, -37.18) * mm});
            skArc(sketch, "E13.20.7", {"start": v(14.44, -37.12) * mm, "mid": v(14.81, -37.28) * mm, "end": v(15.22, -37.24) * mm});
            skArc(sketch, "E13.20.8", {"start": v(13.14, -35.93) * mm, "mid": v(13.76, -36.55) * mm, "end": v(14.44, -37.12) * mm});
            skArc(sketch, "E13.20.9", {"start": v(12.98, -35.65) * mm, "mid": v(13.05, -35.8) * mm, "end": v(13.14, -35.93) * mm});
            skLineSegment(sketch, "E13.20.10", {"start": v(12.98, -35.65) * mm, "end": v(12.59, -34.58) * mm});
            skArc(sketch, "E13.20.11", {"start": v(12.59, -34.58) * mm, "mid": v(12.17, -34.12) * mm, "end": v(11.55, -34.08) * mm});
            skArc(sketch, "E13.21.0", {"start": v(21.3, -29) * mm, "mid": v(20.97, -29.54) * mm, "end": v(21.1, -30.14) * mm});
            skLineSegment(sketch, "E13.21.1", {"start": v(21.76, -31.08) * mm, "end": v(21.1, -30.14) * mm});
            skArc(sketch, "E13.21.2", {"start": v(21.9, -31.37) * mm, "mid": v(21.84, -31.22) * mm, "end": v(21.76, -31.08) * mm});
            skArc(sketch, "E13.21.3", {"start": v(21.9, -31.37) * mm, "mid": v(22.05, -32.24) * mm, "end": v(22.13, -33.12) * mm});
            skArc(sketch, "E13.21.4", {"start": v(21.78, -33.83) * mm, "mid": v(22.04, -33.52) * mm, "end": v(22.13, -33.12) * mm});
            skLineSegment(sketch, "E13.21.5", {"start": v(21.78, -33.83) * mm, "end": v(21.62, -33.94) * mm});
            skLineSegment(sketch, "E13.21.6", {"start": v(21.46, -34.03) * mm, "end": v(21.62, -33.94) * mm});
            skArc(sketch, "E13.21.7", {"start": v(20.66, -34.05) * mm, "mid": v(21.06, -34.14) * mm, "end": v(21.46, -34.03) * mm});
            skArc(sketch, "E13.21.8", {"start": v(19.18, -33.1) * mm, "mid": v(19.9, -33.6) * mm, "end": v(20.66, -34.05) * mm});
            skArc(sketch, "E13.21.9", {"start": v(18.97, -32.86) * mm, "mid": v(19.06, -32.99) * mm, "end": v(19.18, -33.1) * mm});
            skLineSegment(sketch, "E13.21.10", {"start": v(18.97, -32.86) * mm, "end": v(18.4, -31.87) * mm});
            skArc(sketch, "E13.21.11", {"start": v(18.4, -31.87) * mm, "mid": v(17.9, -31.49) * mm, "end": v(17.29, -31.56) * mm});
            skArc(sketch, "E13.22.0", {"start": v(26, -24.87) * mm, "mid": v(25.78, -25.45) * mm, "end": v(26.02, -26.02) * mm});
            skLineSegment(sketch, "E13.22.1", {"start": v(26.83, -26.83) * mm, "end": v(26.02, -26.02) * mm});
            skArc(sketch, "E13.22.2", {"start": v(27, -27.1) * mm, "mid": v(26.93, -26.95) * mm, "end": v(26.83, -26.83) * mm});
            skArc(sketch, "E13.22.3", {"start": v(27, -27.1) * mm, "mid": v(27.31, -27.92) * mm, "end": v(27.54, -28.77) * mm});
            skArc(sketch, "E13.22.4", {"start": v(27.32, -29.53) * mm, "mid": v(27.53, -29.18) * mm, "end": v(27.54, -28.77) * mm});
            skLineSegment(sketch, "E13.22.5", {"start": v(27.32, -29.53) * mm, "end": v(27.19, -29.67) * mm});
            skLineSegment(sketch, "E13.22.6", {"start": v(27.04, -29.79) * mm, "end": v(27.19, -29.67) * mm});
            skArc(sketch, "E13.22.7", {"start": v(26.26, -29.94) * mm, "mid": v(26.67, -29.97) * mm, "end": v(27.04, -29.79) * mm});
            skArc(sketch, "E13.22.8", {"start": v(24.63, -29.26) * mm, "mid": v(25.43, -29.64) * mm, "end": v(26.26, -29.94) * mm});
            skArc(sketch, "E13.22.9", {"start": v(24.39, -29.07) * mm, "mid": v(24.5, -29.18) * mm, "end": v(24.63, -29.26) * mm});
            skLineSegment(sketch, "E13.22.10", {"start": v(24.39, -29.07) * mm, "end": v(23.65, -28.2) * mm});
            skArc(sketch, "E13.22.11", {"start": v(23.65, -28.2) * mm, "mid": v(23.1, -27.9) * mm, "end": v(22.5, -28.08) * mm});
            skArc(sketch, "E13.23.0", {"start": v(29.93, -19.97) * mm, "mid": v(29.8, -20.58) * mm, "end": v(30.14, -21.1) * mm});
            skLineSegment(sketch, "E13.23.1", {"start": v(31.08, -21.76) * mm, "end": v(30.14, -21.1) * mm});
            skArc(sketch, "E13.23.2", {"start": v(31.3, -22) * mm, "mid": v(31.2, -21.87) * mm, "end": v(31.08, -21.76) * mm});
            skArc(sketch, "E13.23.3", {"start": v(31.3, -22) * mm, "mid": v(31.75, -22.75) * mm, "end": v(32.12, -23.55) * mm});
            skArc(sketch, "E13.23.4", {"start": v(32.03, -24.34) * mm, "mid": v(32.18, -23.96) * mm, "end": v(32.12, -23.55) * mm});
            skLineSegment(sketch, "E13.23.5", {"start": v(32.03, -24.34) * mm, "end": v(31.92, -24.5) * mm});
            skLineSegment(sketch, "E13.23.6", {"start": v(31.8, -24.64) * mm, "end": v(31.92, -24.5) * mm});
            skArc(sketch, "E13.23.7", {"start": v(31.06, -24.93) * mm, "mid": v(31.47, -24.88) * mm, "end": v(31.8, -24.64) * mm});
            skArc(sketch, "E13.23.8", {"start": v(29.34, -24.54) * mm, "mid": v(30.2, -24.78) * mm, "end": v(31.06, -24.93) * mm});
            skArc(sketch, "E13.23.9", {"start": v(29.07, -24.39) * mm, "mid": v(29.2, -24.48) * mm, "end": v(29.34, -24.54) * mm});
            skLineSegment(sketch, "E13.23.10", {"start": v(29.07, -24.39) * mm, "end": v(28.2, -23.65) * mm});
            skArc(sketch, "E13.23.11", {"start": v(28.2, -23.65) * mm, "mid": v(27.6, -23.46) * mm, "end": v(27.04, -23.74) * mm});
            skArc(sketch, "E13.24.0", {"start": v(32.94, -14.47) * mm, "mid": v(32.93, -15.1) * mm, "end": v(33.35, -15.55) * mm});
            skLineSegment(sketch, "E13.24.1", {"start": v(34.39, -16.04) * mm, "end": v(33.35, -15.55) * mm});
            skArc(sketch, "E13.24.2", {"start": v(34.64, -16.22) * mm, "mid": v(34.52, -16.12) * mm, "end": v(34.39, -16.04) * mm});
            skArc(sketch, "E13.24.3", {"start": v(34.64, -16.22) * mm, "mid": v(35.21, -16.9) * mm, "end": v(35.72, -17.62) * mm});
            skArc(sketch, "E13.24.4", {"start": v(35.77, -18.4) * mm, "mid": v(35.85, -18) * mm, "end": v(35.72, -17.62) * mm});
            skLineSegment(sketch, "E13.24.5", {"start": v(35.77, -18.4) * mm, "end": v(35.7, -18.58) * mm});
            skLineSegment(sketch, "E13.24.6", {"start": v(35.6, -18.74) * mm, "end": v(35.7, -18.58) * mm});
            skArc(sketch, "E13.24.7", {"start": v(34.92, -19.16) * mm, "mid": v(35.31, -19.04) * mm, "end": v(35.6, -18.74) * mm});
            skArc(sketch, "E13.24.8", {"start": v(33.16, -19.07) * mm, "mid": v(34.04, -19.16) * mm, "end": v(34.92, -19.16) * mm});
            skArc(sketch, "E13.24.9", {"start": v(32.86, -18.97) * mm, "mid": v(33, -19.04) * mm, "end": v(33.16, -19.07) * mm});
            skLineSegment(sketch, "E13.24.10", {"start": v(32.86, -18.97) * mm, "end": v(31.87, -18.4) * mm});
            skArc(sketch, "E13.24.11", {"start": v(31.87, -18.4) * mm, "mid": v(31.25, -18.31) * mm, "end": v(30.75, -18.69) * mm});
            skArc(sketch, "E13.25.0", {"start": v(34.96, -8.53) * mm, "mid": v(35.05, -9.15) * mm, "end": v(35.55, -9.52) * mm});
            skLineSegment(sketch, "E13.25.1", {"start": v(36.65, -9.82) * mm, "end": v(35.55, -9.52) * mm});
            skArc(sketch, "E13.25.2", {"start": v(36.93, -9.96) * mm, "mid": v(36.8, -9.88) * mm, "end": v(36.65, -9.82) * mm});
            skArc(sketch, "E13.25.3", {"start": v(36.93, -9.96) * mm, "mid": v(37.61, -10.52) * mm, "end": v(38.24, -11.15) * mm});
            skArc(sketch, "E13.25.4", {"start": v(38.43, -11.92) * mm, "mid": v(38.43, -11.5) * mm, "end": v(38.24, -11.15) * mm});
            skLineSegment(sketch, "E13.25.5", {"start": v(38.43, -11.92) * mm, "end": v(38.38, -12.1) * mm});
            skLineSegment(sketch, "E13.25.6", {"start": v(38.31, -12.28) * mm, "end": v(38.38, -12.1) * mm});
            skArc(sketch, "E13.25.7", {"start": v(37.72, -12.8) * mm, "mid": v(38.08, -12.62) * mm, "end": v(38.31, -12.28) * mm});
            skArc(sketch, "E13.25.8", {"start": v(35.97, -13.03) * mm, "mid": v(36.85, -12.95) * mm, "end": v(37.72, -12.8) * mm});
            skArc(sketch, "E13.25.9", {"start": v(35.65, -12.98) * mm, "mid": v(35.8, -13.02) * mm, "end": v(35.97, -13.03) * mm});
            skLineSegment(sketch, "E13.25.10", {"start": v(35.65, -12.98) * mm, "end": v(34.58, -12.59) * mm});
            skArc(sketch, "E13.25.11", {"start": v(34.58, -12.59) * mm, "mid": v(33.96, -12.6) * mm, "end": v(33.53, -13.06) * mm});
            skArc(sketch, "E13.26.0", {"start": v(35.9, -2.33) * mm, "mid": v(36.1, -2.92) * mm, "end": v(36.66, -3.2) * mm});
            skLineSegment(sketch, "E13.26.1", {"start": v(37.8, -3.3) * mm, "end": v(36.66, -3.2) * mm});
            skArc(sketch, "E13.26.2", {"start": v(38.1, -3.4) * mm, "mid": v(37.95, -3.34) * mm, "end": v(37.8, -3.3) * mm});
            skArc(sketch, "E13.26.3", {"start": v(38.1, -3.4) * mm, "mid": v(38.87, -3.83) * mm, "end": v(39.6, -4.34) * mm});
            skArc(sketch, "E13.26.4", {"start": v(39.91, -5.06) * mm, "mid": v(39.85, -4.66) * mm, "end": v(39.6, -4.34) * mm});
            skLineSegment(sketch, "E13.26.5", {"start": v(39.91, -5.06) * mm, "end": v(39.9, -5.25) * mm});
            skLineSegment(sketch, "E13.26.6", {"start": v(39.86, -5.44) * mm, "end": v(39.9, -5.25) * mm});
            skArc(sketch, "E13.26.7", {"start": v(39.37, -6.06) * mm, "mid": v(39.7, -5.81) * mm, "end": v(39.86, -5.44) * mm});
            skArc(sketch, "E13.26.8", {"start": v(37.68, -6.58) * mm, "mid": v(38.54, -6.36) * mm, "end": v(39.37, -6.06) * mm});
            skArc(sketch, "E13.26.9", {"start": v(37.37, -6.59) * mm, "mid": v(37.52, -6.6) * mm, "end": v(37.68, -6.58) * mm});
            skLineSegment(sketch, "E13.26.10", {"start": v(37.37, -6.59) * mm, "end": v(36.24, -6.4) * mm});
            skArc(sketch, "E13.26.11", {"start": v(36.24, -6.4) * mm, "mid": v(35.63, -6.52) * mm, "end": v(35.29, -7.04) * mm});
            skArc(sketch, "E13.27.0", {"start": v(35.77, 3.94) * mm, "mid": v(36.06, 3.4) * mm, "end": v(36.66, 3.2) * mm});
            skLineSegment(sketch, "E13.27.1", {"start": v(37.8, 3.3) * mm, "end": v(36.66, 3.2) * mm});
            skArc(sketch, "E13.27.2", {"start": v(38.11, 3.27) * mm, "mid": v(37.96, 3.3) * mm, "end": v(37.8, 3.3) * mm});
            skArc(sketch, "E13.27.3", {"start": v(38.11, 3.27) * mm, "mid": v(38.94, 2.98) * mm, "end": v(39.75, 2.6) * mm});
            skArc(sketch, "E13.27.4", {"start": v(40.18, 1.94) * mm, "mid": v(40.05, 2.33) * mm, "end": v(39.75, 2.6) * mm});
            skLineSegment(sketch, "E13.27.5", {"start": v(40.18, 1.94) * mm, "end": v(40.2, 1.76) * mm});
            skLineSegment(sketch, "E13.27.6", {"start": v(40.2, 1.57) * mm, "end": v(40.2, 1.76) * mm});
            skArc(sketch, "E13.27.7", {"start": v(39.82, 0.87) * mm, "mid": v(40.1, 1.17) * mm, "end": v(40.2, 1.57) * mm});
            skArc(sketch, "E13.27.8", {"start": v(38.25, 0.06) * mm, "mid": v(39.06, 0.43) * mm, "end": v(39.82, 0.87) * mm});
            skArc(sketch, "E13.27.9", {"start": v(37.94, 0) * mm, "mid": v(38.1, 0.02) * mm, "end": v(38.25, 0.06) * mm});
            skLineSegment(sketch, "E13.27.10", {"start": v(37.94, 0) * mm, "end": v(36.8, 0) * mm});
            skArc(sketch, "E13.27.11", {"start": v(36.8, 0) * mm, "mid": v(36.22, -0.24) * mm, "end": v(35.97, -0.8) * mm});
            skArc(sketch, "E13.28.0", {"start": v(34.54, 10.1) * mm, "mid": v(34.93, 9.6) * mm, "end": v(35.55, 9.52) * mm});
            skLineSegment(sketch, "E13.28.1", {"start": v(36.65, 9.82) * mm, "end": v(35.55, 9.52) * mm});
            skArc(sketch, "E13.28.2", {"start": v(36.96, 9.84) * mm, "mid": v(36.8, 9.85) * mm, "end": v(36.65, 9.82) * mm});
            skArc(sketch, "E13.28.3", {"start": v(36.96, 9.84) * mm, "mid": v(37.84, 9.7) * mm, "end": v(38.69, 9.47) * mm});
            skArc(sketch, "E13.28.4", {"start": v(39.24, 8.9) * mm, "mid": v(39.04, 9.25) * mm, "end": v(38.69, 9.47) * mm});
            skLineSegment(sketch, "E13.28.5", {"start": v(39.24, 8.9) * mm, "end": v(39.29, 8.7) * mm});
            skLineSegment(sketch, "E13.28.6", {"start": v(39.32, 8.52) * mm, "end": v(39.29, 8.7) * mm});
            skArc(sketch, "E13.28.7", {"start": v(39.06, 7.77) * mm, "mid": v(39.29, 8.12) * mm, "end": v(39.32, 8.52) * mm});
            skArc(sketch, "E13.28.8", {"start": v(37.66, 6.7) * mm, "mid": v(38.39, 7.2) * mm, "end": v(39.06, 7.77) * mm});
            skArc(sketch, "E13.28.9", {"start": v(37.37, 6.59) * mm, "mid": v(37.52, 6.63) * mm, "end": v(37.66, 6.7) * mm});
            skLineSegment(sketch, "E13.28.10", {"start": v(37.37, 6.59) * mm, "end": v(36.24, 6.4) * mm});
            skArc(sketch, "E13.28.11", {"start": v(36.24, 6.4) * mm, "mid": v(35.71, 6.06) * mm, "end": v(35.57, 5.45) * mm});
            skArc(sketch, "E13.29.0", {"start": v(32.26, 15.93) * mm, "mid": v(32.73, 15.52) * mm, "end": v(33.35, 15.55) * mm});
            skLineSegment(sketch, "E13.29.1", {"start": v(34.39, 16.04) * mm, "end": v(33.35, 15.55) * mm});
            skArc(sketch, "E13.29.2", {"start": v(34.7, 16.11) * mm, "mid": v(34.54, 16.09) * mm, "end": v(34.39, 16.04) * mm});
            skArc(sketch, "E13.29.3", {"start": v(34.7, 16.11) * mm, "mid": v(35.58, 16.12) * mm, "end": v(36.46, 16.04) * mm});
            skArc(sketch, "E13.29.4", {"start": v(37.1, 15.57) * mm, "mid": v(36.84, 15.89) * mm, "end": v(36.46, 16.04) * mm});
            skLineSegment(sketch, "E13.29.5", {"start": v(37.1, 15.57) * mm, "end": v(37.18, 15.4) * mm});
            skLineSegment(sketch, "E13.29.6", {"start": v(37.24, 15.22) * mm, "end": v(37.18, 15.4) * mm});
            skArc(sketch, "E13.29.7", {"start": v(37.12, 14.44) * mm, "mid": v(37.28, 14.81) * mm, "end": v(37.24, 15.22) * mm});
            skArc(sketch, "E13.29.8", {"start": v(35.93, 13.14) * mm, "mid": v(36.55, 13.76) * mm, "end": v(37.12, 14.44) * mm});
            skArc(sketch, "E13.29.9", {"start": v(35.65, 12.98) * mm, "mid": v(35.8, 13.05) * mm, "end": v(35.93, 13.14) * mm});
            skLineSegment(sketch, "E13.29.10", {"start": v(35.65, 12.98) * mm, "end": v(34.58, 12.59) * mm});
            skArc(sketch, "E13.29.11", {"start": v(34.58, 12.59) * mm, "mid": v(34.12, 12.17) * mm, "end": v(34.08, 11.55) * mm});
            skArc(sketch, "E13.30.0", {"start": v(29, 21.3) * mm, "mid": v(29.54, 20.97) * mm, "end": v(30.14, 21.1) * mm});
            skLineSegment(sketch, "E13.30.1", {"start": v(31.08, 21.76) * mm, "end": v(30.14, 21.1) * mm});
            skArc(sketch, "E13.30.2", {"start": v(31.37, 21.9) * mm, "mid": v(31.22, 21.84) * mm, "end": v(31.08, 21.76) * mm});
            skArc(sketch, "E13.30.3", {"start": v(31.37, 21.9) * mm, "mid": v(32.24, 22.05) * mm, "end": v(33.12, 22.13) * mm});
            skArc(sketch, "E13.30.4", {"start": v(33.83, 21.78) * mm, "mid": v(33.52, 22.04) * mm, "end": v(33.12, 22.13) * mm});
            skLineSegment(sketch, "E13.30.5", {"start": v(33.83, 21.78) * mm, "end": v(33.94, 21.62) * mm});
            skLineSegment(sketch, "E13.30.6", {"start": v(34.03, 21.46) * mm, "end": v(33.94, 21.62) * mm});
            skArc(sketch, "E13.30.7", {"start": v(34.05, 20.66) * mm, "mid": v(34.14, 21.06) * mm, "end": v(34.03, 21.46) * mm});
            skArc(sketch, "E13.30.8", {"start": v(33.1, 19.18) * mm, "mid": v(33.6, 19.9) * mm, "end": v(34.05, 20.66) * mm});
            skArc(sketch, "E13.30.9", {"start": v(32.86, 18.97) * mm, "mid": v(32.99, 19.06) * mm, "end": v(33.1, 19.18) * mm});
            skLineSegment(sketch, "E13.30.10", {"start": v(32.86, 18.97) * mm, "end": v(31.87, 18.4) * mm});
            skArc(sketch, "E13.30.11", {"start": v(31.87, 18.4) * mm, "mid": v(31.49, 17.9) * mm, "end": v(31.56, 17.29) * mm});
            skArc(sketch, "E13.31.0", {"start": v(24.87, 26) * mm, "mid": v(25.45, 25.78) * mm, "end": v(26.02, 26.02) * mm});
            skLineSegment(sketch, "E13.31.1", {"start": v(26.83, 26.83) * mm, "end": v(26.02, 26.02) * mm});
            skArc(sketch, "E13.31.2", {"start": v(27.1, 27) * mm, "mid": v(26.95, 26.93) * mm, "end": v(26.83, 26.83) * mm});
            skArc(sketch, "E13.31.3", {"start": v(27.1, 27) * mm, "mid": v(27.92, 27.31) * mm, "end": v(28.77, 27.54) * mm});
            skArc(sketch, "E13.31.4", {"start": v(29.53, 27.32) * mm, "mid": v(29.18, 27.53) * mm, "end": v(28.77, 27.54) * mm});
            skLineSegment(sketch, "E13.31.5", {"start": v(29.53, 27.32) * mm, "end": v(29.67, 27.19) * mm});
            skLineSegment(sketch, "E13.31.6", {"start": v(29.79, 27.04) * mm, "end": v(29.67, 27.19) * mm});
            skArc(sketch, "E13.31.7", {"start": v(29.94, 26.26) * mm, "mid": v(29.97, 26.67) * mm, "end": v(29.79, 27.04) * mm});
            skArc(sketch, "E13.31.8", {"start": v(29.26, 24.63) * mm, "mid": v(29.64, 25.43) * mm, "end": v(29.94, 26.26) * mm});
            skArc(sketch, "E13.31.9", {"start": v(29.07, 24.39) * mm, "mid": v(29.18, 24.5) * mm, "end": v(29.26, 24.63) * mm});
            skLineSegment(sketch, "E13.31.10", {"start": v(29.07, 24.39) * mm, "end": v(28.2, 23.65) * mm});
            skArc(sketch, "E13.31.11", {"start": v(28.2, 23.65) * mm, "mid": v(27.9, 23.1) * mm, "end": v(28.08, 22.5) * mm});
            skArc(sketch, "E13.32.0", {"start": v(19.97, 29.93) * mm, "mid": v(20.58, 29.8) * mm, "end": v(21.1, 30.14) * mm});
            skLineSegment(sketch, "E13.32.1", {"start": v(21.76, 31.08) * mm, "end": v(21.1, 30.14) * mm});
            skArc(sketch, "E13.32.2", {"start": v(22, 31.3) * mm, "mid": v(21.87, 31.2) * mm, "end": v(21.76, 31.08) * mm});
            skArc(sketch, "E13.32.3", {"start": v(22, 31.3) * mm, "mid": v(22.75, 31.75) * mm, "end": v(23.55, 32.12) * mm});
            skArc(sketch, "E13.32.4", {"start": v(24.34, 32.03) * mm, "mid": v(23.96, 32.18) * mm, "end": v(23.55, 32.12) * mm});
            skLineSegment(sketch, "E13.32.5", {"start": v(24.34, 32.03) * mm, "end": v(24.5, 31.92) * mm});
            skLineSegment(sketch, "E13.32.6", {"start": v(24.64, 31.8) * mm, "end": v(24.5, 31.92) * mm});
            skArc(sketch, "E13.32.7", {"start": v(24.93, 31.06) * mm, "mid": v(24.88, 31.47) * mm, "end": v(24.64, 31.8) * mm});
            skArc(sketch, "E13.32.8", {"start": v(24.54, 29.34) * mm, "mid": v(24.78, 30.2) * mm, "end": v(24.93, 31.06) * mm});
            skArc(sketch, "E13.32.9", {"start": v(24.39, 29.07) * mm, "mid": v(24.48, 29.2) * mm, "end": v(24.54, 29.34) * mm});
            skLineSegment(sketch, "E13.32.10", {"start": v(24.39, 29.07) * mm, "end": v(23.65, 28.2) * mm});
            skArc(sketch, "E13.32.11", {"start": v(23.65, 28.2) * mm, "mid": v(23.46, 27.6) * mm, "end": v(23.74, 27.04) * mm});
            skArc(sketch, "E13.33.0", {"start": v(14.47, 32.94) * mm, "mid": v(15.1, 32.93) * mm, "end": v(15.55, 33.35) * mm});
            skLineSegment(sketch, "E13.33.1", {"start": v(16.04, 34.39) * mm, "end": v(15.55, 33.35) * mm});
            skArc(sketch, "E13.33.2", {"start": v(16.22, 34.64) * mm, "mid": v(16.12, 34.52) * mm, "end": v(16.04, 34.39) * mm});
            skArc(sketch, "E13.33.3", {"start": v(16.22, 34.64) * mm, "mid": v(16.9, 35.21) * mm, "end": v(17.62, 35.72) * mm});
            skArc(sketch, "E13.33.4", {"start": v(18.4, 35.77) * mm, "mid": v(18, 35.85) * mm, "end": v(17.62, 35.72) * mm});
            skLineSegment(sketch, "E13.33.5", {"start": v(18.4, 35.77) * mm, "end": v(18.58, 35.7) * mm});
            skLineSegment(sketch, "E13.33.6", {"start": v(18.74, 35.6) * mm, "end": v(18.58, 35.7) * mm});
            skArc(sketch, "E13.33.7", {"start": v(19.16, 34.92) * mm, "mid": v(19.04, 35.31) * mm, "end": v(18.74, 35.6) * mm});
            skArc(sketch, "E13.33.8", {"start": v(19.07, 33.16) * mm, "mid": v(19.16, 34.04) * mm, "end": v(19.16, 34.92) * mm});
            skArc(sketch, "E13.33.9", {"start": v(18.97, 32.86) * mm, "mid": v(19.04, 33) * mm, "end": v(19.07, 33.16) * mm});
            skLineSegment(sketch, "E13.33.10", {"start": v(18.97, 32.86) * mm, "end": v(18.4, 31.87) * mm});
            skArc(sketch, "E13.33.11", {"start": v(18.4, 31.87) * mm, "mid": v(18.31, 31.25) * mm, "end": v(18.69, 30.75) * mm});
            skArc(sketch, "E13.34.0", {"start": v(8.53, 34.96) * mm, "mid": v(9.15, 35.05) * mm, "end": v(9.52, 35.55) * mm});
            skLineSegment(sketch, "E13.34.1", {"start": v(9.82, 36.65) * mm, "end": v(9.52, 35.55) * mm});
            skArc(sketch, "E13.34.2", {"start": v(9.96, 36.93) * mm, "mid": v(9.88, 36.8) * mm, "end": v(9.82, 36.65) * mm});
            skArc(sketch, "E13.34.3", {"start": v(9.96, 36.93) * mm, "mid": v(10.52, 37.61) * mm, "end": v(11.15, 38.24) * mm});
            skArc(sketch, "E13.34.4", {"start": v(11.92, 38.43) * mm, "mid": v(11.5, 38.43) * mm, "end": v(11.15, 38.24) * mm});
            skLineSegment(sketch, "E13.34.5", {"start": v(11.92, 38.43) * mm, "end": v(12.1, 38.38) * mm});
            skLineSegment(sketch, "E13.34.6", {"start": v(12.28, 38.31) * mm, "end": v(12.1, 38.38) * mm});
            skArc(sketch, "E13.34.7", {"start": v(12.8, 37.72) * mm, "mid": v(12.62, 38.08) * mm, "end": v(12.28, 38.31) * mm});
            skArc(sketch, "E13.34.8", {"start": v(13.03, 35.97) * mm, "mid": v(12.95, 36.85) * mm, "end": v(12.8, 37.72) * mm});
            skArc(sketch, "E13.34.9", {"start": v(12.98, 35.65) * mm, "mid": v(13.02, 35.8) * mm, "end": v(13.03, 35.97) * mm});
            skLineSegment(sketch, "E13.34.10", {"start": v(12.98, 35.65) * mm, "end": v(12.59, 34.58) * mm});
            skArc(sketch, "E13.34.11", {"start": v(12.59, 34.58) * mm, "mid": v(12.6, 33.96) * mm, "end": v(13.06, 33.53) * mm});
            skArc(sketch, "E13.35.0", {"start": v(2.33, 35.9) * mm, "mid": v(2.92, 36.1) * mm, "end": v(3.2, 36.66) * mm});
            skLineSegment(sketch, "E13.35.1", {"start": v(3.3, 37.8) * mm, "end": v(3.2, 36.66) * mm});
            skArc(sketch, "E13.35.2", {"start": v(3.4, 38.1) * mm, "mid": v(3.34, 37.95) * mm, "end": v(3.3, 37.8) * mm});
            skArc(sketch, "E13.35.3", {"start": v(3.4, 38.1) * mm, "mid": v(3.83, 38.87) * mm, "end": v(4.34, 39.6) * mm});
            skArc(sketch, "E13.35.4", {"start": v(5.06, 39.91) * mm, "mid": v(4.66, 39.85) * mm, "end": v(4.34, 39.6) * mm});
            skLineSegment(sketch, "E13.35.5", {"start": v(5.06, 39.91) * mm, "end": v(5.25, 39.9) * mm});
            skLineSegment(sketch, "E13.35.6", {"start": v(5.44, 39.86) * mm, "end": v(5.25, 39.9) * mm});
            skArc(sketch, "E13.35.7", {"start": v(6.06, 39.37) * mm, "mid": v(5.81, 39.7) * mm, "end": v(5.44, 39.86) * mm});
            skArc(sketch, "E13.35.8", {"start": v(6.58, 37.68) * mm, "mid": v(6.36, 38.54) * mm, "end": v(6.06, 39.37) * mm});
            skArc(sketch, "E13.35.9", {"start": v(6.59, 37.37) * mm, "mid": v(6.6, 37.52) * mm, "end": v(6.58, 37.68) * mm});
            skLineSegment(sketch, "E13.35.10", {"start": v(6.59, 37.37) * mm, "end": v(6.4, 36.24) * mm});
            skArc(sketch, "E13.35.11", {"start": v(6.4, 36.24) * mm, "mid": v(6.52, 35.63) * mm, "end": v(7.04, 35.29) * mm});
            skArc(sketch, "E14.trimOffspring", {"start": v(-10.1, 34.54) * mm, "mid": v(-10.82, 34.32) * mm, "end": v(-11.55, 34.08) * mm});
            skArc(sketch, "E15.trimOffspring", {"start": v(-15.93, 32.26) * mm, "mid": v(-16.62, 31.92) * mm, "end": v(-17.29, 31.56) * mm});
            skArc(sketch, "E16.trimOffspring", {"start": v(-21.3, 29) * mm, "mid": v(-21.9, 28.55) * mm, "end": v(-22.5, 28.08) * mm});
            skArc(sketch, "E17.trimOffspring", {"start": v(-26, 24.87) * mm, "mid": v(-26.53, 24.3) * mm, "end": v(-27.04, 23.74) * mm});
            skArc(sketch, "E18.trimOffspring", {"start": v(-29.93, 19.97) * mm, "mid": v(-30.35, 19.33) * mm, "end": v(-30.75, 18.69) * mm});
            skArc(sketch, "E19.trimOffspring", {"start": v(-32.94, 14.47) * mm, "mid": v(-33.24, 13.77) * mm, "end": v(-33.53, 13.06) * mm});
            skArc(sketch, "E20.trimOffspring", {"start": v(-34.96, 8.53) * mm, "mid": v(-35.13, 7.79) * mm, "end": v(-35.29, 7.04) * mm});
            skArc(sketch, "E21.trimOffspring", {"start": v(2.33, 35.9) * mm, "mid": v(1.57, 35.95) * mm, "end": v(0.8, 35.97) * mm});
            skArc(sketch, "E22.trimOffspring", {"start": v(14.47, 32.94) * mm, "mid": v(13.77, 33.24) * mm, "end": v(13.06, 33.53) * mm});
            skArc(sketch, "E23.trimOffspring", {"start": v(19.97, 29.93) * mm, "mid": v(19.33, 30.35) * mm, "end": v(18.69, 30.75) * mm});
            skArc(sketch, "E24.trimOffspring", {"start": v(8.53, 34.96) * mm, "mid": v(7.79, 35.13) * mm, "end": v(7.04, 35.29) * mm});
            skArc(sketch, "E25.trimOffspring", {"start": v(24.87, 26) * mm, "mid": v(24.3, 26.53) * mm, "end": v(23.74, 27.04) * mm});
            skArc(sketch, "E26.trimOffspring", {"start": v(29, 21.3) * mm, "mid": v(28.55, 21.9) * mm, "end": v(28.08, 22.5) * mm});
            skArc(sketch, "E27.trimOffspring", {"start": v(-35.9, 2.33) * mm, "mid": v(-35.95, 1.57) * mm, "end": v(-35.97, 0.8) * mm});
            skArc(sketch, "E28.trimOffspring", {"start": v(-35.77, -3.94) * mm, "mid": v(-35.68, -4.7) * mm, "end": v(-35.57, -5.45) * mm});
            skArc(sketch, "E29.trimOffspring", {"start": v(-34.54, -10.1) * mm, "mid": v(-34.32, -10.82) * mm, "end": v(-34.08, -11.55) * mm});
            skArc(sketch, "E30.trimOffspring", {"start": v(-32.26, -15.93) * mm, "mid": v(-31.92, -16.62) * mm, "end": v(-31.56, -17.29) * mm});
            skArc(sketch, "E31.trimOffspring", {"start": v(-29, -21.3) * mm, "mid": v(-28.55, -21.9) * mm, "end": v(-28.08, -22.5) * mm});
            skArc(sketch, "E32.trimOffspring", {"start": v(-24.87, -26) * mm, "mid": v(-24.3, -26.53) * mm, "end": v(-23.74, -27.04) * mm});
            skArc(sketch, "E33.trimOffspring", {"start": v(-19.97, -29.93) * mm, "mid": v(-19.33, -30.35) * mm, "end": v(-18.69, -30.75) * mm});
            skArc(sketch, "E34.trimOffspring", {"start": v(-14.47, -32.94) * mm, "mid": v(-13.77, -33.24) * mm, "end": v(-13.06, -33.53) * mm});
            skArc(sketch, "E35.trimOffspring", {"start": v(-8.53, -34.96) * mm, "mid": v(-7.79, -35.13) * mm, "end": v(-7.04, -35.29) * mm});
            skArc(sketch, "E36.trimOffspring", {"start": v(-2.33, -35.9) * mm, "mid": v(-1.57, -35.95) * mm, "end": v(-0.8, -35.97) * mm});
            skArc(sketch, "E37.trimOffspring", {"start": v(3.94, -35.77) * mm, "mid": v(4.7, -35.68) * mm, "end": v(5.45, -35.57) * mm});
            skArc(sketch, "E38.trimOffspring", {"start": v(10.1, -34.54) * mm, "mid": v(10.82, -34.32) * mm, "end": v(11.55, -34.08) * mm});
            skArc(sketch, "E39.trimOffspring", {"start": v(15.93, -32.26) * mm, "mid": v(16.62, -31.92) * mm, "end": v(17.29, -31.56) * mm});
            skArc(sketch, "E40.trimOffspring", {"start": v(21.3, -29) * mm, "mid": v(21.9, -28.55) * mm, "end": v(22.5, -28.08) * mm});
            skArc(sketch, "E41.trimOffspring", {"start": v(26, -24.87) * mm, "mid": v(26.53, -24.3) * mm, "end": v(27.04, -23.74) * mm});
            skArc(sketch, "E42.trimOffspring", {"start": v(29.93, -19.97) * mm, "mid": v(30.35, -19.33) * mm, "end": v(30.75, -18.69) * mm});
            skArc(sketch, "E43.trimOffspring", {"start": v(32.94, -14.47) * mm, "mid": v(33.24, -13.77) * mm, "end": v(33.53, -13.06) * mm});
            skArc(sketch, "E44.trimOffspring", {"start": v(34.96, -8.53) * mm, "mid": v(35.13, -7.79) * mm, "end": v(35.29, -7.04) * mm});
            skArc(sketch, "E45.trimOffspring", {"start": v(35.9, -2.33) * mm, "mid": v(35.95, -1.57) * mm, "end": v(35.97, -0.8) * mm});
            skArc(sketch, "E46.trimOffspring", {"start": v(32.26, 15.93) * mm, "mid": v(31.92, 16.62) * mm, "end": v(31.56, 17.29) * mm});
            skArc(sketch, "E47.trimOffspring", {"start": v(34.54, 10.1) * mm, "mid": v(34.32, 10.82) * mm, "end": v(34.08, 11.55) * mm});
            skArc(sketch, "E48.trimOffspring", {"start": v(35.77, 3.94) * mm, "mid": v(35.68, 4.7) * mm, "end": v(35.57, 5.45) * mm});
            skSolve(sketch);
        }
        {
            var Q0;
            Q0 = qSketchRegion(id + "F0", true);
            extrude(context, id + "F1", {"entities" : qUnion([Q0]), "depth" : 12.7 * mm});
        }
        {
            var Q0;
            Q0=makeQuery(id+"F1.opExtrude","CAP_FACE",FACE,{"disambiguationData":[OSD([sQuery(id+"F0.wireOp",EDGE,"E0"),sQuery(id+"F0.wireOp",EDGE,"E1"),sQuery(id+"F0.wireOp",EDGE,"E2"),sQuery(id+"F0.wireOp",EDGE,"E3.trimOffspring"),sQuery(id+"F0.wireOp",EDGE,"E4.MirrorCS"),sQuery(id+"F0.wireOp",EDGE,"E5.MirrorCS"),sQuery(id+"F0.wireOp",EDGE,"E6.MirrorCS"),sQuery(id+"F0.wireOp",EDGE,"E7.filletArc"),sQuery(id+"F0.wireOp",EDGE,"E8.filletArc"),sQuery(id+"F0.wireOp",EDGE,"E9.filletArc"),sQuery(id+"F0.wireOp",EDGE,"E10.filletArc"),sQuery(id+"F0.wireOp",EDGE,"E11.filletArc"),sQuery(id+"F0.wireOp",EDGE,"E12.filletArc"),sQuery(id+"F0.wireOp",EDGE,"E13.1.0"),sQuery(id+"F0.wireOp",EDGE,"E13.1.1"),sQuery(id+"F0.wireOp",EDGE,"E13.1.2"),sQuery(id+"F0.wireOp",EDGE,"E13.1.3"),sQuery(id+"F0.wireOp",EDGE,"E13.1.4"),sQuery(id+"F0.wireOp",EDGE,"E13.1.5"),sQuery(id+"F0.wireOp",EDGE,"E13.1.6"),sQuery(id+"F0.wireOp",EDGE,"E13.1.7"),sQuery(id+"F0.wireOp",EDGE,"E13.1.8"),sQuery(id+"F0.wireOp",EDGE,"E13.1.9"),sQuery(id+"F0.wireOp",EDGE,"E13.1.10"),sQuery(id+"F0.wireOp",EDGE,"E13.1.11"),sQuery(id+"F0.wireOp",EDGE,"E13.2.0"),sQuery(id+"F0.wireOp",EDGE,"E13.2.1"),sQuery(id+"F0.wireOp",EDGE,"E13.2.2"),sQuery(id+"F0.wireOp",EDGE,"E13.2.3"),sQuery(id+"F0.wireOp",EDGE,"E13.2.4"),sQuery(id+"F0.wireOp",EDGE,"E13.2.5"),sQuery(id+"F0.wireOp",EDGE,"E13.2.6"),sQuery(id+"F0.wireOp",EDGE,"E13.2.7"),sQuery(id+"F0.wireOp",EDGE,"E13.2.8"),sQuery(id+"F0.wireOp",EDGE,"E13.2.9"),sQuery(id+"F0.wireOp",EDGE,"E13.2.10"),sQuery(id+"F0.wireOp",EDGE,"E13.2.11"),sQuery(id+"F0.wireOp",EDGE,"E13.3.0"),sQuery(id+"F0.wireOp",EDGE,"E13.3.1"),sQuery(id+"F0.wireOp",EDGE,"E13.3.2"),sQuery(id+"F0.wireOp",EDGE,"E13.3.3"),sQuery(id+"F0.wireOp",EDGE,"E13.3.4"),sQuery(id+"F0.wireOp",EDGE,"E13.3.5"),sQuery(id+"F0.wireOp",EDGE,"E13.3.6"),sQuery(id+"F0.wireOp",EDGE,"E13.3.7"),sQuery(id+"F0.wireOp",EDGE,"E13.3.8"),sQuery(id+"F0.wireOp",EDGE,"E13.3.9"),sQuery(id+"F0.wireOp",EDGE,"E13.3.10"),sQuery(id+"F0.wireOp",EDGE,"E13.3.11"),sQuery(id+"F0.wireOp",EDGE,"E13.4.0"),sQuery(id+"F0.wireOp",EDGE,"E13.4.1"),sQuery(id+"F0.wireOp",EDGE,"E13.4.2"),sQuery(id+"F0.wireOp",EDGE,"E13.4.3"),sQuery(id+"F0.wireOp",EDGE,"E13.4.4"),sQuery(id+"F0.wireOp",EDGE,"E13.4.5"),sQuery(id+"F0.wireOp",EDGE,"E13.4.6"),sQuery(id+"F0.wireOp",EDGE,"E13.4.7"),sQuery(id+"F0.wireOp",EDGE,"E13.4.8"),sQuery(id+"F0.wireOp",EDGE,"E13.4.9"),sQuery(id+"F0.wireOp",EDGE,"E13.4.10"),sQuery(id+"F0.wireOp",EDGE,"E13.4.11"),sQuery(id+"F0.wireOp",EDGE,"E13.5.0"),sQuery(id+"F0.wireOp",EDGE,"E13.5.1"),sQuery(id+"F0.wireOp",EDGE,"E13.5.2"),sQuery(id+"F0.wireOp",EDGE,"E13.5.3"),sQuery(id+"F0.wireOp",EDGE,"E13.5.4"),sQuery(id+"F0.wireOp",EDGE,"E13.5.5"),sQuery(id+"F0.wireOp",EDGE,"E13.5.6"),sQuery(id+"F0.wireOp",EDGE,"E13.5.7"),sQuery(id+"F0.wireOp",EDGE,"E13.5.8"),sQuery(id+"F0.wireOp",EDGE,"E13.5.9"),sQuery(id+"F0.wireOp",EDGE,"E13.5.10"),sQuery(id+"F0.wireOp",EDGE,"E13.5.11"),sQuery(id+"F0.wireOp",EDGE,"E13.6.0"),sQuery(id+"F0.wireOp",EDGE,"E13.6.1"),sQuery(id+"F0.wireOp",EDGE,"E13.6.2"),sQuery(id+"F0.wireOp",EDGE,"E13.6.3"),sQuery(id+"F0.wireOp",EDGE,"E13.6.4"),sQuery(id+"F0.wireOp",EDGE,"E13.6.5"),sQuery(id+"F0.wireOp",EDGE,"E13.6.6"),sQuery(id+"F0.wireOp",EDGE,"E13.6.7"),sQuery(id+"F0.wireOp",EDGE,"E13.6.8"),sQuery(id+"F0.wireOp",EDGE,"E13.6.9"),sQuery(id+"F0.wireOp",EDGE,"E13.6.10"),sQuery(id+"F0.wireOp",EDGE,"E13.6.11"),sQuery(id+"F0.wireOp",EDGE,"E13.7.0"),sQuery(id+"F0.wireOp",EDGE,"E13.7.1"),sQuery(id+"F0.wireOp",EDGE,"E13.7.2"),sQuery(id+"F0.wireOp",EDGE,"E13.7.3"),sQuery(id+"F0.wireOp",EDGE,"E13.7.4"),sQuery(id+"F0.wireOp",EDGE,"E13.7.5"),sQuery(id+"F0.wireOp",EDGE,"E13.7.6"),sQuery(id+"F0.wireOp",EDGE,"E13.7.7"),sQuery(id+"F0.wireOp",EDGE,"E13.7.8"),sQuery(id+"F0.wireOp",EDGE,"E13.7.9"),sQuery(id+"F0.wireOp",EDGE,"E13.7.10"),sQuery(id+"F0.wireOp",EDGE,"E13.7.11"),sQuery(id+"F0.wireOp",EDGE,"E13.8.0"),sQuery(id+"F0.wireOp",EDGE,"E13.8.1"),sQuery(id+"F0.wireOp",EDGE,"E13.8.2"),sQuery(id+"F0.wireOp",EDGE,"E13.8.3"),sQuery(id+"F0.wireOp",EDGE,"E13.8.4"),sQuery(id+"F0.wireOp",EDGE,"E13.8.5"),sQuery(id+"F0.wireOp",EDGE,"E13.8.6"),sQuery(id+"F0.wireOp",EDGE,"E13.8.7"),sQuery(id+"F0.wireOp",EDGE,"E13.8.8"),sQuery(id+"F0.wireOp",EDGE,"E13.8.9"),sQuery(id+"F0.wireOp",EDGE,"E13.8.10"),sQuery(id+"F0.wireOp",EDGE,"E13.8.11"),sQuery(id+"F0.wireOp",EDGE,"E13.9.0"),sQuery(id+"F0.wireOp",EDGE,"E13.9.1"),sQuery(id+"F0.wireOp",EDGE,"E13.9.2"),sQuery(id+"F0.wireOp",EDGE,"E13.9.3"),sQuery(id+"F0.wireOp",EDGE,"E13.9.4"),sQuery(id+"F0.wireOp",EDGE,"E13.9.5"),sQuery(id+"F0.wireOp",EDGE,"E13.9.6"),sQuery(id+"F0.wireOp",EDGE,"E13.9.7"),sQuery(id+"F0.wireOp",EDGE,"E13.9.8"),sQuery(id+"F0.wireOp",EDGE,"E13.9.9"),sQuery(id+"F0.wireOp",EDGE,"E13.9.10"),sQuery(id+"F0.wireOp",EDGE,"E13.9.11"),sQuery(id+"F0.wireOp",EDGE,"E13.10.0"),sQuery(id+"F0.wireOp",EDGE,"E13.10.1"),sQuery(id+"F0.wireOp",EDGE,"E13.10.2"),sQuery(id+"F0.wireOp",EDGE,"E13.10.3"),sQuery(id+"F0.wireOp",EDGE,"E13.10.4"),sQuery(id+"F0.wireOp",EDGE,"E13.10.5"),sQuery(id+"F0.wireOp",EDGE,"E13.10.6"),sQuery(id+"F0.wireOp",EDGE,"E13.10.7"),sQuery(id+"F0.wireOp",EDGE,"E13.10.8"),sQuery(id+"F0.wireOp",EDGE,"E13.10.9"),sQuery(id+"F0.wireOp",EDGE,"E13.10.10"),sQuery(id+"F0.wireOp",EDGE,"E13.10.11"),sQuery(id+"F0.wireOp",EDGE,"E13.11.0"),sQuery(id+"F0.wireOp",EDGE,"E13.11.1"),sQuery(id+"F0.wireOp",EDGE,"E13.11.2"),sQuery(id+"F0.wireOp",EDGE,"E13.11.3"),sQuery(id+"F0.wireOp",EDGE,"E13.11.4"),sQuery(id+"F0.wireOp",EDGE,"E13.11.5"),sQuery(id+"F0.wireOp",EDGE,"E13.11.6"),sQuery(id+"F0.wireOp",EDGE,"E13.11.7"),sQuery(id+"F0.wireOp",EDGE,"E13.11.8"),sQuery(id+"F0.wireOp",EDGE,"E13.11.9"),sQuery(id+"F0.wireOp",EDGE,"E13.11.10"),sQuery(id+"F0.wireOp",EDGE,"E13.11.11"),sQuery(id+"F0.wireOp",EDGE,"E13.12.0"),sQuery(id+"F0.wireOp",EDGE,"E13.12.1"),sQuery(id+"F0.wireOp",EDGE,"E13.12.2"),sQuery(id+"F0.wireOp",EDGE,"E13.12.3"),sQuery(id+"F0.wireOp",EDGE,"E13.12.4"),sQuery(id+"F0.wireOp",EDGE,"E13.12.5"),sQuery(id+"F0.wireOp",EDGE,"E13.12.6"),sQuery(id+"F0.wireOp",EDGE,"E13.12.7"),sQuery(id+"F0.wireOp",EDGE,"E13.12.8"),sQuery(id+"F0.wireOp",EDGE,"E13.12.9"),sQuery(id+"F0.wireOp",EDGE,"E13.12.10"),sQuery(id+"F0.wireOp",EDGE,"E13.12.11"),sQuery(id+"F0.wireOp",EDGE,"E13.13.0"),sQuery(id+"F0.wireOp",EDGE,"E13.13.1"),sQuery(id+"F0.wireOp",EDGE,"E13.13.2"),sQuery(id+"F0.wireOp",EDGE,"E13.13.3"),sQuery(id+"F0.wireOp",EDGE,"E13.13.4"),sQuery(id+"F0.wireOp",EDGE,"E13.13.5"),sQuery(id+"F0.wireOp",EDGE,"E13.13.6"),sQuery(id+"F0.wireOp",EDGE,"E13.13.7"),sQuery(id+"F0.wireOp",EDGE,"E13.13.8"),sQuery(id+"F0.wireOp",EDGE,"E13.13.9"),sQuery(id+"F0.wireOp",EDGE,"E13.13.10"),sQuery(id+"F0.wireOp",EDGE,"E13.13.11"),sQuery(id+"F0.wireOp",EDGE,"E13.14.0"),sQuery(id+"F0.wireOp",EDGE,"E13.14.1"),sQuery(id+"F0.wireOp",EDGE,"E13.14.2"),sQuery(id+"F0.wireOp",EDGE,"E13.14.3"),sQuery(id+"F0.wireOp",EDGE,"E13.14.4"),sQuery(id+"F0.wireOp",EDGE,"E13.14.5"),sQuery(id+"F0.wireOp",EDGE,"E13.14.6"),sQuery(id+"F0.wireOp",EDGE,"E13.14.7"),sQuery(id+"F0.wireOp",EDGE,"E13.14.8"),sQuery(id+"F0.wireOp",EDGE,"E13.14.9"),sQuery(id+"F0.wireOp",EDGE,"E13.14.10"),sQuery(id+"F0.wireOp",EDGE,"E13.14.11"),sQuery(id+"F0.wireOp",EDGE,"E13.15.0"),sQuery(id+"F0.wireOp",EDGE,"E13.15.1"),sQuery(id+"F0.wireOp",EDGE,"E13.15.2"),sQuery(id+"F0.wireOp",EDGE,"E13.15.3"),sQuery(id+"F0.wireOp",EDGE,"E13.15.4"),sQuery(id+"F0.wireOp",EDGE,"E13.15.5"),sQuery(id+"F0.wireOp",EDGE,"E13.15.6"),sQuery(id+"F0.wireOp",EDGE,"E13.15.7"),sQuery(id+"F0.wireOp",EDGE,"E13.15.8"),sQuery(id+"F0.wireOp",EDGE,"E13.15.9"),sQuery(id+"F0.wireOp",EDGE,"E13.15.10"),sQuery(id+"F0.wireOp",EDGE,"E13.15.11"),sQuery(id+"F0.wireOp",EDGE,"E13.16.0"),sQuery(id+"F0.wireOp",EDGE,"E13.16.1"),sQuery(id+"F0.wireOp",EDGE,"E13.16.2"),sQuery(id+"F0.wireOp",EDGE,"E13.16.3"),sQuery(id+"F0.wireOp",EDGE,"E13.16.4"),sQuery(id+"F0.wireOp",EDGE,"E13.16.5"),sQuery(id+"F0.wireOp",EDGE,"E13.16.6"),sQuery(id+"F0.wireOp",EDGE,"E13.16.7"),sQuery(id+"F0.wireOp",EDGE,"E13.16.8"),sQuery(id+"F0.wireOp",EDGE,"E13.16.9"),sQuery(id+"F0.wireOp",EDGE,"E13.16.10"),sQuery(id+"F0.wireOp",EDGE,"E13.16.11"),sQuery(id+"F0.wireOp",EDGE,"E13.17.0"),sQuery(id+"F0.wireOp",EDGE,"E13.17.1"),sQuery(id+"F0.wireOp",EDGE,"E13.17.2"),sQuery(id+"F0.wireOp",EDGE,"E13.17.3"),sQuery(id+"F0.wireOp",EDGE,"E13.17.4"),sQuery(id+"F0.wireOp",EDGE,"E13.17.5"),sQuery(id+"F0.wireOp",EDGE,"E13.17.6"),sQuery(id+"F0.wireOp",EDGE,"E13.17.7"),sQuery(id+"F0.wireOp",EDGE,"E13.17.8"),sQuery(id+"F0.wireOp",EDGE,"E13.17.9"),sQuery(id+"F0.wireOp",EDGE,"E13.17.10"),sQuery(id+"F0.wireOp",EDGE,"E13.17.11"),sQuery(id+"F0.wireOp",EDGE,"E13.18.0"),sQuery(id+"F0.wireOp",EDGE,"E13.18.1"),sQuery(id+"F0.wireOp",EDGE,"E13.18.2"),sQuery(id+"F0.wireOp",EDGE,"E13.18.3"),sQuery(id+"F0.wireOp",EDGE,"E13.18.4"),sQuery(id+"F0.wireOp",EDGE,"E13.18.5"),sQuery(id+"F0.wireOp",EDGE,"E13.18.6"),sQuery(id+"F0.wireOp",EDGE,"E13.18.7"),sQuery(id+"F0.wireOp",EDGE,"E13.18.8"),sQuery(id+"F0.wireOp",EDGE,"E13.18.9"),sQuery(id+"F0.wireOp",EDGE,"E13.18.10"),sQuery(id+"F0.wireOp",EDGE,"E13.18.11"),sQuery(id+"F0.wireOp",EDGE,"E13.19.0"),sQuery(id+"F0.wireOp",EDGE,"E13.19.1"),sQuery(id+"F0.wireOp",EDGE,"E13.19.2"),sQuery(id+"F0.wireOp",EDGE,"E13.19.3"),sQuery(id+"F0.wireOp",EDGE,"E13.19.4"),sQuery(id+"F0.wireOp",EDGE,"E13.19.5"),sQuery(id+"F0.wireOp",EDGE,"E13.19.6"),sQuery(id+"F0.wireOp",EDGE,"E13.19.7"),sQuery(id+"F0.wireOp",EDGE,"E13.19.8"),sQuery(id+"F0.wireOp",EDGE,"E13.19.9"),sQuery(id+"F0.wireOp",EDGE,"E13.19.10"),sQuery(id+"F0.wireOp",EDGE,"E13.19.11"),sQuery(id+"F0.wireOp",EDGE,"E13.20.0"),sQuery(id+"F0.wireOp",EDGE,"E13.20.1"),sQuery(id+"F0.wireOp",EDGE,"E13.20.2"),sQuery(id+"F0.wireOp",EDGE,"E13.20.3"),sQuery(id+"F0.wireOp",EDGE,"E13.20.4"),sQuery(id+"F0.wireOp",EDGE,"E13.20.5"),sQuery(id+"F0.wireOp",EDGE,"E13.20.6"),sQuery(id+"F0.wireOp",EDGE,"E13.20.7"),sQuery(id+"F0.wireOp",EDGE,"E13.20.8"),sQuery(id+"F0.wireOp",EDGE,"E13.20.9"),sQuery(id+"F0.wireOp",EDGE,"E13.20.10"),sQuery(id+"F0.wireOp",EDGE,"E13.20.11"),sQuery(id+"F0.wireOp",EDGE,"E13.21.0"),sQuery(id+"F0.wireOp",EDGE,"E13.21.1"),sQuery(id+"F0.wireOp",EDGE,"E13.21.2"),sQuery(id+"F0.wireOp",EDGE,"E13.21.3"),sQuery(id+"F0.wireOp",EDGE,"E13.21.4"),sQuery(id+"F0.wireOp",EDGE,"E13.21.5"),sQuery(id+"F0.wireOp",EDGE,"E13.21.6"),sQuery(id+"F0.wireOp",EDGE,"E13.21.7"),sQuery(id+"F0.wireOp",EDGE,"E13.21.8"),sQuery(id+"F0.wireOp",EDGE,"E13.21.9"),sQuery(id+"F0.wireOp",EDGE,"E13.21.10"),sQuery(id+"F0.wireOp",EDGE,"E13.21.11"),sQuery(id+"F0.wireOp",EDGE,"E13.22.0"),sQuery(id+"F0.wireOp",EDGE,"E13.22.1"),sQuery(id+"F0.wireOp",EDGE,"E13.22.2"),sQuery(id+"F0.wireOp",EDGE,"E13.22.3"),sQuery(id+"F0.wireOp",EDGE,"E13.22.4"),sQuery(id+"F0.wireOp",EDGE,"E13.22.5"),sQuery(id+"F0.wireOp",EDGE,"E13.22.6"),sQuery(id+"F0.wireOp",EDGE,"E13.22.7"),sQuery(id+"F0.wireOp",EDGE,"E13.22.8"),sQuery(id+"F0.wireOp",EDGE,"E13.22.9"),sQuery(id+"F0.wireOp",EDGE,"E13.22.10"),sQuery(id+"F0.wireOp",EDGE,"E13.22.11"),sQuery(id+"F0.wireOp",EDGE,"E13.23.0"),sQuery(id+"F0.wireOp",EDGE,"E13.23.1"),sQuery(id+"F0.wireOp",EDGE,"E13.23.2"),sQuery(id+"F0.wireOp",EDGE,"E13.23.3"),sQuery(id+"F0.wireOp",EDGE,"E13.23.4"),sQuery(id+"F0.wireOp",EDGE,"E13.23.5"),sQuery(id+"F0.wireOp",EDGE,"E13.23.6"),sQuery(id+"F0.wireOp",EDGE,"E13.23.7"),sQuery(id+"F0.wireOp",EDGE,"E13.23.8"),sQuery(id+"F0.wireOp",EDGE,"E13.23.9"),sQuery(id+"F0.wireOp",EDGE,"E13.23.10"),sQuery(id+"F0.wireOp",EDGE,"E13.23.11"),sQuery(id+"F0.wireOp",EDGE,"E13.24.0"),sQuery(id+"F0.wireOp",EDGE,"E13.24.1"),sQuery(id+"F0.wireOp",EDGE,"E13.24.2"),sQuery(id+"F0.wireOp",EDGE,"E13.24.3"),sQuery(id+"F0.wireOp",EDGE,"E13.24.4"),sQuery(id+"F0.wireOp",EDGE,"E13.24.5"),sQuery(id+"F0.wireOp",EDGE,"E13.24.6"),sQuery(id+"F0.wireOp",EDGE,"E13.24.7"),sQuery(id+"F0.wireOp",EDGE,"E13.24.8"),sQuery(id+"F0.wireOp",EDGE,"E13.24.9"),sQuery(id+"F0.wireOp",EDGE,"E13.24.10"),sQuery(id+"F0.wireOp",EDGE,"E13.24.11"),sQuery(id+"F0.wireOp",EDGE,"E13.25.0"),sQuery(id+"F0.wireOp",EDGE,"E13.25.1"),sQuery(id+"F0.wireOp",EDGE,"E13.25.2"),sQuery(id+"F0.wireOp",EDGE,"E13.25.3"),sQuery(id+"F0.wireOp",EDGE,"E13.25.4"),sQuery(id+"F0.wireOp",EDGE,"E13.25.5"),sQuery(id+"F0.wireOp",EDGE,"E13.25.6"),sQuery(id+"F0.wireOp",EDGE,"E13.25.7"),sQuery(id+"F0.wireOp",EDGE,"E13.25.8"),sQuery(id+"F0.wireOp",EDGE,"E13.25.9"),sQuery(id+"F0.wireOp",EDGE,"E13.25.10"),sQuery(id+"F0.wireOp",EDGE,"E13.25.11"),sQuery(id+"F0.wireOp",EDGE,"E13.26.0"),sQuery(id+"F0.wireOp",EDGE,"E13.26.1"),sQuery(id+"F0.wireOp",EDGE,"E13.26.2"),sQuery(id+"F0.wireOp",EDGE,"E13.26.3"),sQuery(id+"F0.wireOp",EDGE,"E13.26.4"),sQuery(id+"F0.wireOp",EDGE,"E13.26.5"),sQuery(id+"F0.wireOp",EDGE,"E13.26.6"),sQuery(id+"F0.wireOp",EDGE,"E13.26.7"),sQuery(id+"F0.wireOp",EDGE,"E13.26.8"),sQuery(id+"F0.wireOp",EDGE,"E13.26.9"),sQuery(id+"F0.wireOp",EDGE,"E13.26.10"),sQuery(id+"F0.wireOp",EDGE,"E13.26.11"),sQuery(id+"F0.wireOp",EDGE,"E13.27.0"),sQuery(id+"F0.wireOp",EDGE,"E13.27.1"),sQuery(id+"F0.wireOp",EDGE,"E13.27.2"),sQuery(id+"F0.wireOp",EDGE,"E13.27.3"),sQuery(id+"F0.wireOp",EDGE,"E13.27.4"),sQuery(id+"F0.wireOp",EDGE,"E13.27.5"),sQuery(id+"F0.wireOp",EDGE,"E13.27.6"),sQuery(id+"F0.wireOp",EDGE,"E13.27.7"),sQuery(id+"F0.wireOp",EDGE,"E13.27.8"),sQuery(id+"F0.wireOp",EDGE,"E13.27.9"),sQuery(id+"F0.wireOp",EDGE,"E13.27.10"),sQuery(id+"F0.wireOp",EDGE,"E13.27.11"),sQuery(id+"F0.wireOp",EDGE,"E13.28.0"),sQuery(id+"F0.wireOp",EDGE,"E13.28.1"),sQuery(id+"F0.wireOp",EDGE,"E13.28.2"),sQuery(id+"F0.wireOp",EDGE,"E13.28.3"),sQuery(id+"F0.wireOp",EDGE,"E13.28.4"),sQuery(id+"F0.wireOp",EDGE,"E13.28.5"),sQuery(id+"F0.wireOp",EDGE,"E13.28.6"),sQuery(id+"F0.wireOp",EDGE,"E13.28.7"),sQuery(id+"F0.wireOp",EDGE,"E13.28.8"),sQuery(id+"F0.wireOp",EDGE,"E13.28.9"),sQuery(id+"F0.wireOp",EDGE,"E13.28.10"),sQuery(id+"F0.wireOp",EDGE,"E13.28.11"),sQuery(id+"F0.wireOp",EDGE,"E13.29.0"),sQuery(id+"F0.wireOp",EDGE,"E13.29.1"),sQuery(id+"F0.wireOp",EDGE,"E13.29.2"),sQuery(id+"F0.wireOp",EDGE,"E13.29.3"),sQuery(id+"F0.wireOp",EDGE,"E13.29.4"),sQuery(id+"F0.wireOp",EDGE,"E13.29.5"),sQuery(id+"F0.wireOp",EDGE,"E13.29.6"),sQuery(id+"F0.wireOp",EDGE,"E13.29.7"),sQuery(id+"F0.wireOp",EDGE,"E13.29.8"),sQuery(id+"F0.wireOp",EDGE,"E13.29.9"),sQuery(id+"F0.wireOp",EDGE,"E13.29.10"),sQuery(id+"F0.wireOp",EDGE,"E13.29.11"),sQuery(id+"F0.wireOp",EDGE,"E13.30.0"),sQuery(id+"F0.wireOp",EDGE,"E13.30.1"),sQuery(id+"F0.wireOp",EDGE,"E13.30.2"),sQuery(id+"F0.wireOp",EDGE,"E13.30.3"),sQuery(id+"F0.wireOp",EDGE,"E13.30.4"),sQuery(id+"F0.wireOp",EDGE,"E13.30.5"),sQuery(id+"F0.wireOp",EDGE,"E13.30.6"),sQuery(id+"F0.wireOp",EDGE,"E13.30.7"),sQuery(id+"F0.wireOp",EDGE,"E13.30.8"),sQuery(id+"F0.wireOp",EDGE,"E13.30.9"),sQuery(id+"F0.wireOp",EDGE,"E13.30.10"),sQuery(id+"F0.wireOp",EDGE,"E13.30.11"),sQuery(id+"F0.wireOp",EDGE,"E13.31.0"),sQuery(id+"F0.wireOp",EDGE,"E13.31.1"),sQuery(id+"F0.wireOp",EDGE,"E13.31.2"),sQuery(id+"F0.wireOp",EDGE,"E13.31.3"),sQuery(id+"F0.wireOp",EDGE,"E13.31.4"),sQuery(id+"F0.wireOp",EDGE,"E13.31.5"),sQuery(id+"F0.wireOp",EDGE,"E13.31.6"),sQuery(id+"F0.wireOp",EDGE,"E13.31.7"),sQuery(id+"F0.wireOp",EDGE,"E13.31.8"),sQuery(id+"F0.wireOp",EDGE,"E13.31.9"),sQuery(id+"F0.wireOp",EDGE,"E13.31.10"),sQuery(id+"F0.wireOp",EDGE,"E13.31.11"),sQuery(id+"F0.wireOp",EDGE,"E13.32.0"),sQuery(id+"F0.wireOp",EDGE,"E13.32.1"),sQuery(id+"F0.wireOp",EDGE,"E13.32.2"),sQuery(id+"F0.wireOp",EDGE,"E13.32.3"),sQuery(id+"F0.wireOp",EDGE,"E13.32.4"),sQuery(id+"F0.wireOp",EDGE,"E13.32.5"),sQuery(id+"F0.wireOp",EDGE,"E13.32.6"),sQuery(id+"F0.wireOp",EDGE,"E13.32.7"),sQuery(id+"F0.wireOp",EDGE,"E13.32.8"),sQuery(id+"F0.wireOp",EDGE,"E13.32.9"),sQuery(id+"F0.wireOp",EDGE,"E13.32.10"),sQuery(id+"F0.wireOp",EDGE,"E13.32.11"),sQuery(id+"F0.wireOp",EDGE,"E13.33.0"),sQuery(id+"F0.wireOp",EDGE,"E13.33.1"),sQuery(id+"F0.wireOp",EDGE,"E13.33.2"),sQuery(id+"F0.wireOp",EDGE,"E13.33.3"),sQuery(id+"F0.wireOp",EDGE,"E13.33.4"),sQuery(id+"F0.wireOp",EDGE,"E13.33.5"),sQuery(id+"F0.wireOp",EDGE,"E13.33.6"),sQuery(id+"F0.wireOp",EDGE,"E13.33.7"),sQuery(id+"F0.wireOp",EDGE,"E13.33.8"),sQuery(id+"F0.wireOp",EDGE,"E13.33.9"),sQuery(id+"F0.wireOp",EDGE,"E13.33.10"),sQuery(id+"F0.wireOp",EDGE,"E13.33.11"),sQuery(id+"F0.wireOp",EDGE,"E13.34.0"),sQuery(id+"F0.wireOp",EDGE,"E13.34.1"),sQuery(id+"F0.wireOp",EDGE,"E13.34.2"),sQuery(id+"F0.wireOp",EDGE,"E13.34.3"),sQuery(id+"F0.wireOp",EDGE,"E13.34.4"),sQuery(id+"F0.wireOp",EDGE,"E13.34.5"),sQuery(id+"F0.wireOp",EDGE,"E13.34.6"),sQuery(id+"F0.wireOp",EDGE,"E13.34.7"),sQuery(id+"F0.wireOp",EDGE,"E13.34.8"),sQuery(id+"F0.wireOp",EDGE,"E13.34.9"),sQuery(id+"F0.wireOp",EDGE,"E13.34.10"),sQuery(id+"F0.wireOp",EDGE,"E13.34.11"),sQuery(id+"F0.wireOp",EDGE,"E13.35.0"),sQuery(id+"F0.wireOp",EDGE,"E13.35.1"),sQuery(id+"F0.wireOp",EDGE,"E13.35.2"),sQuery(id+"F0.wireOp",EDGE,"E13.35.3"),sQuery(id+"F0.wireOp",EDGE,"E13.35.4"),sQuery(id+"F0.wireOp",EDGE,"E13.35.5"),sQuery(id+"F0.wireOp",EDGE,"E13.35.6"),sQuery(id+"F0.wireOp",EDGE,"E13.35.7"),sQuery(id+"F0.wireOp",EDGE,"E13.35.8"),sQuery(id+"F0.wireOp",EDGE,"E13.35.9"),sQuery(id+"F0.wireOp",EDGE,"E13.35.10"),sQuery(id+"F0.wireOp",EDGE,"E13.35.11"),sQuery(id+"F0.wireOp",EDGE,"E14.trimOffspring"),sQuery(id+"F0.wireOp",EDGE,"E15.trimOffspring"),sQuery(id+"F0.wireOp",EDGE,"E16.trimOffspring"),sQuery(id+"F0.wireOp",EDGE,"E17.trimOffspring"),sQuery(id+"F0.wireOp",EDGE,"E18.trimOffspring"),sQuery(id+"F0.wireOp",EDGE,"E19.trimOffspring"),sQuery(id+"F0.wireOp",EDGE,"E20.trimOffspring"),sQuery(id+"F0.wireOp",EDGE,"E21.trimOffspring"),sQuery(id+"F0.wireOp",EDGE,"E22.trimOffspring"),sQuery(id+"F0.wireOp",EDGE,"E23.trimOffspring"),sQuery(id+"F0.wireOp",EDGE,"E24.trimOffspring"),sQuery(id+"F0.wireOp",EDGE,"E25.trimOffspring"),sQuery(id+"F0.wireOp",EDGE,"E26.trimOffspring"),sQuery(id+"F0.wireOp",EDGE,"E27.trimOffspring"),sQuery(id+"F0.wireOp",EDGE,"E28.trimOffspring"),sQuery(id+"F0.wireOp",EDGE,"E29.trimOffspring"),sQuery(id+"F0.wireOp",EDGE,"E30.trimOffspring"),sQuery(id+"F0.wireOp",EDGE,"E31.trimOffspring"),sQuery(id+"F0.wireOp",EDGE,"E32.trimOffspring"),sQuery(id+"F0.wireOp",EDGE,"E33.trimOffspring"),sQuery(id+"F0.wireOp",EDGE,"E34.trimOffspring"),sQuery(id+"F0.wireOp",EDGE,"E35.trimOffspring"),sQuery(id+"F0.wireOp",EDGE,"E36.trimOffspring"),sQuery(id+"F0.wireOp",EDGE,"E37.trimOffspring"),sQuery(id+"F0.wireOp",EDGE,"E38.trimOffspring"),sQuery(id+"F0.wireOp",EDGE,"E39.trimOffspring"),sQuery(id+"F0.wireOp",EDGE,"E40.trimOffspring"),sQuery(id+"F0.wireOp",EDGE,"E41.trimOffspring"),sQuery(id+"F0.wireOp",EDGE,"E42.trimOffspring"),sQuery(id+"F0.wireOp",EDGE,"E43.trimOffspring"),sQuery(id+"F0.wireOp",EDGE,"E44.trimOffspring"),sQuery(id+"F0.wireOp",EDGE,"E45.trimOffspring"),sQuery(id+"F0.wireOp",EDGE,"E46.trimOffspring"),sQuery(id+"F0.wireOp",EDGE,"E47.trimOffspring"),sQuery(id+"F0.wireOp",EDGE,"E48.trimOffspring")])],"isStart":false});
            var sketch = newSketch(context, id + "F2", { "sketchPlane" : qUnion([Q0])});
            skCircle(sketch, "E49", {"center": v(0, 0) * mm, "radius": 3.17 * mm});
            skSolve(sketch);
        }
        {
            var Q0;
            Q0=makeQuery(id+"F2.imprint","IMPRINT",FACE,{"disambiguationData":[TD([[makeQuery(id+"F2.imprint","IMPRINT",EDGE,{"derivedFrom":sQuery(id+"F2.wireOp",EDGE,"E49")}),1.0]])]});
            extrude(context, id + "F3", {"entities" : qUnion([Q0]), "operationType" : NewBodyOperationType.REMOVE, "endBound" : BoundingType.THROUGH_ALL, "oppositeDirection" : true, "depth" : 25.4 * mm});
        }
    });
